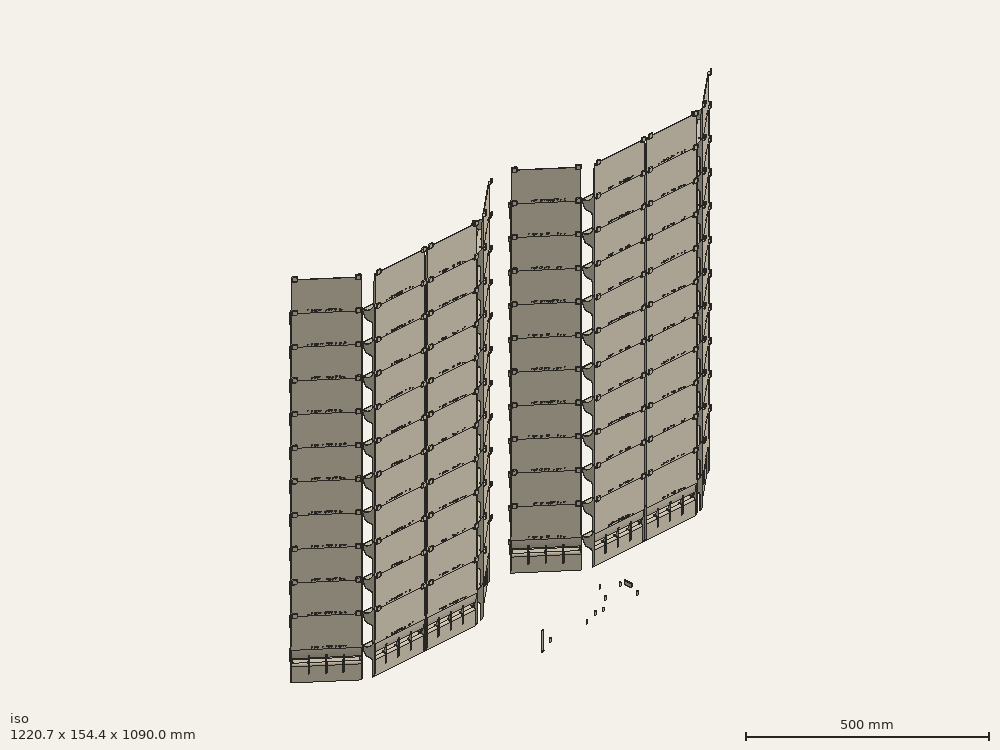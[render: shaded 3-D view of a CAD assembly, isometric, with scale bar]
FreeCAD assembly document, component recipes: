
FREECAD ASSEMBLY — COMPONENT RECIPES ("composit_stand8")

This assembly document has 28 components, labeled P0..P27 below (a component is one placed body or linked part). 26 of them carry a construction recipe — the FreeCAD feature program that regenerates the part from scratch, quoted from this document or its linked companion documents; the rest are supplied as boundary geometry only. No exploded tour is included for this assembly.
NOTE — this tour is split across 2 documents so each fits a 32k-token context. This is document 1: the component sections continue in the remaining 1 document, each repeating the header above.
COMPONENT P0 — recipe-attached ("sink", modeled in this document).
Construction recipe (the document's own serialized feature program — sketch geometry with constraints, then the solid features built on it; lengths are millimeters unless a unit is written):

FEATURE [PartDesign::SubShapeBinder] Binder001
  BindCopyOnChange = 0
  BindMode = 0
  ClaimChildren = true
  Context = -> Body003 [Binder001.]
  Fuse = false
  MakeFace = true
  OffsetFill = false
  OffsetIntersection = false
  OffsetJoinType = 0
  OffsetOpenResult = false
  PartialLoad = false
  Relative = false
  Support = -> [Sketch]
  _Version = 2
FEATURE [PartDesign::CoordinateSystem] Local_CS
  AttacherType = Attacher::AttachEngine3D
  AttachmentOffset = pos=(0,0,0) rot=(0,1,0;1.5708rad)
  MapMode = 7
  Placement = pos=(164.635,-1.4e-14,0) rot=(0.889126,0.323616,0.323616;1.68804rad)
FEATURE [Sketcher::SketchObject] Sketch005  label="sink_side_line"
  ExternalGeometry = -> [Binder001]
  FullyConstrained = true
  MapMode = 5
  Placement = pos=(164.635,-2.8e-14,0) rot=(0.889126,0.323616,0.323616;1.68804rad)
  sketch-geometry (1):
    g0: LineSegment StartX=-2.84e-14 StartY=0 StartZ=0 EndX=202.244 EndY=20 EndZ=0
  constraints (4):
    c: Coincident(g0,g-3)
    c: Vertical(g0,g-3)
    c: DistanceY(g0) = 20  'height'
    c: Angle(g0) = 0.0985699  'angle'
FEATURE [Sketcher::SketchObject] Sketch006  label="sink_front_bend_sketch"
  ExternalGeometry = -> [Sketch005]
  FullyConstrained = true
  MapMode = 5
  Placement = pos=(0,0,0) rot=(0.57735,0.57735,0.57735;2.0944rad)
  sketch-geometry (3):
    g0: LineSegment StartX=0 StartY=2.91403 StartZ=0 EndX=-1.83e-14 EndY=0 EndZ=0
    g1: LineSegment StartX=-1.83e-14 StartY=0 StartZ=0 EndX=2.88014 EndY=0.443099 EndZ=0
    g2: ArcOfCircle CenterX=2.5 CenterY=2.91403 CenterZ=0 NormalX=0 NormalY=0 NormalZ=1 AngleXU=0 Radius=2.5 StartAngle=3.14159 EndAngle=4.86504
  constraints (8):
    c: PointOnObject(g0,g-2)
    c: Coincident(g0,g-3)
    c: Coincident(g0,g1)
    c: PointOnObject(g1,g-3)
    c: Tangent(g2,g1) = -1.5708
    c: Tangent(g2,g0) = -1.5708
    c: Radius(g2) = 2.5
    c: Angle(g1) = 0.152649  'angle'
FEATURE [Sketcher::SketchObject] Sketch007
  ExternalGeometry = -> [Binder001]
  FullyConstrained = true
  MapMode = 7
  Placement = pos=(164.635,-8.5e-14,-4e-15) rot=(0.846388,-0.394677,-0.357572;1.83324rad)
  sketch-geometry (3):
    g0: ArcOfCircle CenterX=-2.5 CenterY=2.81034 CenterZ=0 NormalX=0 NormalY=0 NormalZ=1 AngleXU=0 Radius=2.5 StartAngle=4.59564 EndAngle=6.28319
    g1: LineSegment StartX=-2.79121 StartY=0.327355 StartZ=0 EndX=0 EndY=0 EndZ=0
    g2: LineSegment StartX=0 StartY=0 StartZ=0 EndX=0 EndY=2.81034 EndZ=0
  constraints (7):
    c: PointOnObject(g0,g-2)
    c: Coincident(g1,g-1)
    c: Coincident(g2,g1)
    c: Tangent(g2,g0) = -1.5708
    c: Tangent(g1,g0) = -1.5708
    c: PointOnObject(g0,g-3)
    c: Radius(g0) = 2.5
FEATURE [PartDesign::CoordinateSystem] Local_CS001
  AttacherType = Attacher::AttachEngine3D
  AttachmentOffset = pos=(0,0,0) rot=(1,0,0;0.152649rad)
  MapMode = 5
  Placement = pos=(0,0,0) rot=(1,0,0;0.152649rad)
  expr: .AttachmentOffset.Rotation.Angle = <<sink_front_bend_sketch>>.Constraints.angle
FEATURE [Sketcher::SketchObject] Sketch008  label="sink_plane_sketch"
  ExternalGeometry = -> [Sketch006,Sketch005,Sketch007]
  FullyConstrained = true
  MapMode = 5
  Placement = pos=(0,0,0) rot=(1,0,0;0.152649rad)
  sketch-geometry (4):
    g0: LineSegment StartX=-163.725 StartY=2.91403 StartZ=0 EndX=163.725 EndY=2.91403 EndZ=0
    g1: LineSegment StartX=163.725 StartY=2.91403 StartZ=0 EndX=317.576 EndY=133.529 EndZ=0
    g2: LineSegment StartX=317.576 StartY=133.529 StartZ=0 EndX=-317.576 EndY=133.529 EndZ=0
    g3: LineSegment StartX=-317.576 StartY=133.529 StartZ=0 EndX=-163.725 EndY=2.91403 EndZ=0
  constraints (14):
    c: Coincident(g0,g1)
    c: Coincident(g1,g2)
    c: Coincident(g2,g3)
    c: Coincident(g3,g0)
    c: Symmetric(g0,g0,g-2)
    c: Symmetric(g2,g1,g-2)
    c: Parallel(g1,g-4)
    c: PointOnObject(g-5,g1)
    c: PointOnObject(g-3,g0)
    c: Distance(g1) = 201.818  'rigth_side'
    c: Distance(g0) = 327.45  'front'
    c: Distance(g2) = 635.153  'end'
    c: Distance(g3) = 201.818  'left_side'
    c: DistanceY(g-4,g1) = 2
FEATURE [Sketcher::SketchObject] Sketch009
  ExternalGeometry = -> [Sketch006]
  FullyConstrained = true
  MapMode = 2
  Placement = pos=(0,0,0) rot=(0.57735,0.57735,0.57735;2.0944rad)
  sketch-geometry (4):
    g0: ArcOfCircle CenterX=2.5 CenterY=2.91403 CenterZ=0 NormalX=0 NormalY=0 NormalZ=1 AngleXU=0 Radius=2.5 StartAngle=3.14159 EndAngle=4.86504
    g1: LineSegment StartX=2.88014 StartY=0.443099 StartZ=0 EndX=2.80411 EndY=0.937285 EndZ=0
    g2: LineSegment StartX=1.1302e-12 StartY=2.91403 StartZ=0 EndX=0.5 EndY=2.91403 EndZ=0
    g3: ArcOfCircle CenterX=2.5 CenterY=2.91403 CenterZ=0 NormalX=0 NormalY=0 NormalZ=1 AngleXU=0 Radius=2 StartAngle=3.14159 EndAngle=4.86504
  constraints (10):
    c: Coincident(g0,g-3)
    c: Tangent(g0,g-3) = -1.5708
    c: Coincident(g0,g1)
    c: Coincident(g0,g2)
    c: Coincident(g3,g0)
    c: Coincident(g3,g2)
    c: Coincident(g3,g1)
    c: Perpendicular(g3,g1)
    c: Perpendicular(g3,g2)
    c: Distance(g1) = 0.5
FEATURE [Sketcher::SketchObject] Sketch010
  ExternalGeometry = -> [Sketch007]
  FullyConstrained = true
  MapMode = 7
  Placement = pos=(163.725,2.88014,0.443099) rot=(0.846388,-0.394677,-0.357572;1.83324rad)
  sketch-geometry (4):
    g0: ArcOfCircle CenterX=0.291206 CenterY=2.48298 CenterZ=0 NormalX=0 NormalY=0 NormalZ=1 AngleXU=0 Radius=2.5 StartAngle=4.59564 EndAngle=6.28319
    g1: LineSegment StartX=-2.56e-14 StartY=2.7e-15 StartZ=0 EndX=0.0582413 EndY=0.496596 EndZ=0
    g2: LineSegment StartX=2.79121 StartY=2.48298 StartZ=0 EndX=2.29121 EndY=2.48298 EndZ=0
    g3: ArcOfCircle CenterX=0.291206 CenterY=2.48298 CenterZ=0 NormalX=0 NormalY=0 NormalZ=1 AngleXU=0 Radius=2 StartAngle=4.59564 EndAngle=6.28319
  constraints (10):
    c: Coincident(g0,g-3)
    c: Tangent(g0,g-3) = -1.5708
    c: Coincident(g1,g0)
    c: Coincident(g2,g0)
    c: Coincident(g3,g0)
    c: Coincident(g3,g1)
    c: Coincident(g3,g2)
    c: Perpendicular(g0,g1)
    c: Perpendicular(g0,g2)
    c: Distance(g1) = 0.5
FEATURE [Sketcher::SketchObject] Sketch011
  ExternalGeometry = -> [Sketch008]
  FullyConstrained = true
  MapMode = 7
  Placement = pos=(-163.725,2.88014,0.443099) rot=(-0.298783,0.640743,0.707232;3.7787rad)
  sketch-geometry (4):
    g0: ArcOfCircle CenterX=0.291206 CenterY=2.48298 CenterZ=0 NormalX=0 NormalY=0 NormalZ=1 AngleXU=0 Radius=2 StartAngle=4.59564 EndAngle=6.28319
    g1: ArcOfCircle CenterX=0.291206 CenterY=2.48298 CenterZ=0 NormalX=0 NormalY=0 NormalZ=1 AngleXU=0 Radius=2.5 StartAngle=4.59564 EndAngle=6.28319
    g2: LineSegment StartX=-4e-16 StartY=0 StartZ=0 EndX=0.0582413 EndY=0.496596 EndZ=0
    g3: LineSegment StartX=2.29121 StartY=2.48298 StartZ=0 EndX=2.79121 EndY=2.48298 EndZ=0
  constraints (12):
    c: Coincident(g1,g0)
    c: Coincident(g1,g-1)
    c: Coincident(g2,g1)
    c: Coincident(g2,g0)
    c: Coincident(g3,g0)
    c: Coincident(g3,g1)
    c: Perpendicular(g0,g3)
    c: Perpendicular(g0,g2)
    c: Perpendicular(g2,g-3)
    c: Horizontal(g3)
    c: Radius(g0) = 2
    c: Distance(g2) = 0.5
FEATURE [PartDesign::Pad] Pad
  Direction = (0,-0.152057,0.988372)
  Length = 0.5
  Length2 = 10
  Placement = pos=(0,0,0) rot=(1,0,0;0.152649rad)
  Profile = -> Sketch008
  ReferenceAxis = -> Sketch008 [N_Axis]
  Suppressed = false
  Type = 0
FEATURE [PartDesign::Pad] Pad001
  BaseFeature = -> Pad
  Direction = (-0.762326,-0.639667,-0.0984104)
  Length = 201.818
  Length2 = 10
  Placement = pos=(0,0,0) rot=(1,0,0;0.152649rad)
  Profile = -> Sketch010
  ReferenceAxis = -> Sketch010 [N_Axis]
  Reversed = true
  Suppressed = false
  Type = 0
  expr: Length = <<sink_plane_sketch>>.Constraints.rigth_side
FEATURE [PartDesign::Pad] Pad002
  BaseFeature = -> Pad001
  Direction = (-0.762326,0.639667,0.0984104)
  Length = 201.818
  Length2 = 10
  Placement = pos=(0,0,0) rot=(1,0,0;0.152649rad)
  Profile = -> Sketch011
  ReferenceAxis = -> Sketch011 [N_Axis]
  Suppressed = false
  Type = 0
  expr: Length = <<sink_plane_sketch>>.Constraints.left_side
FEATURE [PartDesign::Pad] Pad003
  BaseFeature = -> Pad002
  Direction = (1,0,0)
  Length = 327.45
  Length2 = 10
  Midplane = true
  Placement = pos=(0,0,0) rot=(1,0,0;0.152649rad)
  Profile = -> Sketch009
  ReferenceAxis = -> Sketch009 [N_Axis]
  Suppressed = false
  Type = 0
  expr: Length = <<sink_plane_sketch>>.Constraints.front
FEATURE [Sketcher::SketchObject] Sketch013
  ExternalGeometry = -> [Sketch008,Sketch009]
  FullyConstrained = true
  MapMode = 5
  Placement = pos=(0,0,0) rot=(1,0,0;1.5708rad)
  sketch-geometry (6):
    g0: LineSegment StartX=-163.725 StartY=2.91403 StartZ=0 EndX=-163.725 EndY=80 EndZ=0
    g1: LineSegment StartX=-163.725 StartY=80 StartZ=0 EndX=163.725 EndY=80 EndZ=0
    g2: LineSegment StartX=163.725 StartY=80 StartZ=0 EndX=163.725 EndY=2.91403 EndZ=0
    g3: LineSegment StartX=163.725 StartY=2.91403 StartZ=0 EndX=-163.725 EndY=2.91403 EndZ=0
    g4: LineSegment StartX=-163.725 StartY=0.443099 StartZ=0 EndX=-163.725 EndY=2.91403 EndZ=0
    g5: LineSegment StartX=163.725 StartY=0.443099 StartZ=0 EndX=163.725 EndY=2.91403 EndZ=0
  constraints (16):
    c: Vertical(g0)
    c: Coincident(g0,g1)
    c: Horizontal(g1)
    c: Coincident(g1,g2)
    c: Vertical(g2)
    c: Coincident(g2,g3)
    c: Coincident(g3,g0)
    c: Horizontal(g3)
    c: PointOnObject(g-4,g3)
    c: Coincident(g4,g-3)
    c: Coincident(g4,g0)
    c: Perpendicular(g3,g4)
    c: Coincident(g5,g-3)
    c: Coincident(g5,g2)
    c: Perpendicular(g3,g5)
    c: DistanceY(g1) = 80
FEATURE [Sketcher::SketchObject] Sketch012
  ExternalGeometry = -> [Sketch008,Sketch010,Sketch013]
  FullyConstrained = true
  MapMode = 5
  Placement = pos=(164.635,-2.8e-14,0) rot=(0.889126,0.323616,0.323616;1.68804rad)
  sketch-geometry (4):
    g0: LineSegment StartX=0.909926 StartY=2.91403 StartZ=0 EndX=201.749 EndY=22.775 EndZ=0
    g1: LineSegment StartX=0.909926 StartY=2.91403 StartZ=0 EndX=0.909926 EndY=80 EndZ=0
    g2: LineSegment StartX=0.909926 StartY=80 StartZ=0 EndX=201.749 EndY=80 EndZ=0
    g3: LineSegment StartX=201.749 StartY=80 StartZ=0 EndX=201.749 EndY=22.775 EndZ=0
  constraints (11):
    c: Coincident(g0,g-4)
    c: Parallel(g-3,g0)
    c: Equal(g0,g-3)
    c: Coincident(g0,g1)
    c: Vertical(g1)
    c: Coincident(g1,g2)
    c: Horizontal(g2)
    c: Coincident(g2,g3)
    c: Coincident(g3,g0)
    c: Vertical(g3)
    c: Horizontal(g-5,g1)
FEATURE [PartDesign::Pad] Pad004
  BaseFeature = -> Pad003
  Direction = (0,-1,2e-16)
  Length = 0.5
  Length2 = 10
  Placement = pos=(0,0,0) rot=(1,0,0;0.152649rad)
  Profile = -> Sketch013
  ReferenceAxis = -> Sketch013 [N_Axis]
  Reversed = true
  Suppressed = false
  Type = 0
FEATURE [PartDesign::Pad] Pad005
  BaseFeature = -> Pad004
  Direction = (0.642788,-0.766044,-2e-16)
  Length = 0.5
  Length2 = 10
  Placement = pos=(0,0,0) rot=(1,0,0;0.152649rad)
  Profile = -> Sketch012
  ReferenceAxis = -> Sketch012 [N_Axis]
  Reversed = true
  Suppressed = false
  Type = 0
FEATURE [Sketcher::SketchObject] Sketch014
  ExternalGeometry = -> [Binder001]
  FullyConstrained = true
  MapMode = 5
  sketch-geometry (1):
    g0: LineSegment StartX=-319.563 StartY=130 StartZ=0 EndX=-164.635 EndY=0 EndZ=0
  constraints (2):
    c: Symmetric(g0,g-3,g-2)
    c: Symmetric(g0,g-3,g-2)
FEATURE [PartDesign::CoordinateSystem] Local_CS003
  AttacherType = Attacher::AttachEngine3D
  AttachmentOffset = pos=(0,0,0) rot=(0,1,0;1.5708rad)
  MapMode = 7
  Placement = pos=(-164.635,-1.4e-14,0) rot=(0.889126,-0.323616,-0.323616;1.68804rad)
FEATURE [Sketcher::SketchObject] Sketch015
  ExternalGeometry = -> [Sketch008,Sketch011,Sketch013]
  FullyConstrained = true
  MapMode = 5
  Placement = pos=(-164.635,-2.8e-14,0) rot=(0.889126,-0.323616,-0.323616;1.68804rad)
  sketch-geometry (5):
    g0: LineSegment StartX=-201.749 StartY=22.775 StartZ=0 EndX=-0.909926 EndY=2.91403 EndZ=0
    g1: LineSegment StartX=-0.909926 StartY=2.91403 StartZ=0 EndX=-0.909926 EndY=80 EndZ=0
    g2: LineSegment StartX=-0.909926 StartY=80 StartZ=0 EndX=-201.749 EndY=80 EndZ=0
    g3: LineSegment StartX=-201.749 StartY=80 StartZ=0 EndX=-201.749 EndY=22.775 EndZ=0
    g4: LineSegment StartX=-201.993 StartY=20.3041 StartZ=0 EndX=-201.749 EndY=22.775 EndZ=0
  constraints (13):
    c: Coincident(g0,g-4)
    c: Coincident(g1,g0)
    c: Vertical(g1)
    c: Coincident(g1,g2)
    c: Horizontal(g2)
    c: Coincident(g2,g3)
    c: Coincident(g3,g0)
    c: Vertical(g3)
    c: Coincident(g4,g-3)
    c: Coincident(g4,g0)
    c: Perpendicular(g-3,g4)
    c: Parallel(g-3,g0)
    c: Horizontal(g1,g-5)
FEATURE [PartDesign::Pad] Pad006
  BaseFeature = -> Pad005
  Direction = (-0.642788,-0.766044,-2e-16)
  Length = 0.5
  Length2 = 10
  Placement = pos=(0,0,0) rot=(1,0,0;0.152649rad)
  Profile = -> Sketch015
  ReferenceAxis = -> Sketch015 [N_Axis]
  Reversed = true
  Suppressed = false
  Type = 0
FEATURE [Sketcher::SketchObject] Sketch016
  ExternalGeometry = -> [Pad006]
  FullyConstrained = true
  MapMode = 5
  Placement = pos=(0,0,0) rot=(1,0,0;0.152649rad)
  sketch-geometry (28):
    g0: LineSegment StartX=0 StartY=2 StartZ=0 EndX=40.9313 EndY=2 EndZ=0
    g1: LineSegment StartX=40.9313 StartY=2 StartZ=0 EndX=81.8625 EndY=2 EndZ=0
    g2: LineSegment StartX=81.8625 StartY=2 StartZ=0 EndX=122.794 EndY=2 EndZ=0
    g3: LineSegment StartX=122.794 StartY=2 StartZ=0 EndX=163.725 EndY=2 EndZ=0
    g4: ArcOfCircle CenterX=-17 CenterY=2 CenterZ=0 NormalX=0 NormalY=0 NormalZ=1 AngleXU=0 Radius=3 StartAngle=1.5708 EndAngle=4.71239
    g5: ArcOfCircle CenterX=17 CenterY=2 CenterZ=0 NormalX=0 NormalY=0 NormalZ=1 AngleXU=0 Radius=3 StartAngle=4.71239 EndAngle=7.85398
    g6: LineSegment StartX=-17 StartY=5 StartZ=0 EndX=17 EndY=5 EndZ=0
    g7: LineSegment StartX=-17 StartY=-1 StartZ=0 EndX=17 EndY=-1 EndZ=0
    g8: GeomPoint X=-20 Y=2 Z=0
    g9: GeomPoint X=20 Y=2 Z=0
    g10: ArcOfCircle CenterX=106 CenterY=2 CenterZ=0 NormalX=0 NormalY=0 NormalZ=1 AngleXU=0 Radius=3 StartAngle=1.5708 EndAngle=4.71239
    g11: ArcOfCircle CenterX=140 CenterY=2 CenterZ=0 NormalX=0 NormalY=0 NormalZ=1 AngleXU=0 Radius=3 StartAngle=4.71239 EndAngle=7.85398
    g12: LineSegment StartX=106 StartY=5 StartZ=0 EndX=140 EndY=5 EndZ=0
    g13: LineSegment StartX=106 StartY=-1 StartZ=0 EndX=140 EndY=-1 EndZ=0
    g14: ArcOfCircle CenterX=-140 CenterY=2 CenterZ=0 NormalX=0 NormalY=0 NormalZ=1 AngleXU=0 Radius=3 StartAngle=1.5708 EndAngle=4.71239
    g15: ArcOfCircle CenterX=-106 CenterY=2 CenterZ=0 NormalX=0 NormalY=0 NormalZ=1 AngleXU=0 Radius=3 StartAngle=4.71239 EndAngle=7.85398
    g16: LineSegment StartX=-140 StartY=5 StartZ=0 EndX=-106 EndY=5 EndZ=0
    g17: LineSegment StartX=-140 StartY=-1 StartZ=0 EndX=-106 EndY=-1 EndZ=0
    g18: ArcOfCircle CenterX=-78.5 CenterY=2 CenterZ=0 NormalX=0 NormalY=0 NormalZ=1 AngleXU=0 Radius=3 StartAngle=1.5708 EndAngle=4.71239
    g19: ArcOfCircle CenterX=-44.5 CenterY=2 CenterZ=0 NormalX=0 NormalY=0 NormalZ=1 AngleXU=0 Radius=3 StartAngle=4.71239 EndAngle=7.85398
    g20: LineSegment StartX=-78.5 StartY=5 StartZ=0 EndX=-44.5 EndY=5 EndZ=0
    g21: LineSegment StartX=-78.5 StartY=-1 StartZ=0 EndX=-44.5 EndY=-1 EndZ=0
    g22: ArcOfCircle CenterX=44.5 CenterY=2 CenterZ=0 NormalX=0 NormalY=0 NormalZ=1 AngleXU=0 Radius=3 StartAngle=1.5708 EndAngle=4.71239
    g23: ArcOfCircle CenterX=78.5 CenterY=2 CenterZ=0 NormalX=0 NormalY=0 NormalZ=1 AngleXU=0 Radius=3 StartAngle=4.71239 EndAngle=7.85398
    g24: LineSegment StartX=44.5 StartY=5 StartZ=0 EndX=78.5 EndY=5 EndZ=0
    g25: LineSegment StartX=44.5 StartY=-1 StartZ=0 EndX=78.5 EndY=-1 EndZ=0
    g26: LineSegment StartX=17 StartY=-1 StartZ=0 EndX=44.5 EndY=-1 EndZ=0
    g27: LineSegment StartX=78.5 StartY=-1 StartZ=0 EndX=106 EndY=-1 EndZ=0
  constraints (67):
    c: PointOnObject(g0,g-2)
    c: Coincident(g0,g1)
    c: Horizontal(g1)
    c: Coincident(g1,g2)
    c: Coincident(g2,g3)
    c: Horizontal(g3)
    c: Vertical(g-3,g3)
    c: Horizontal(g0)
    c: Equal(g0,g1)
    c: Equal(g1,g2)
    c: Equal(g2,g3)
    c: DistanceY(g0) = 2
    c: Horizontal(g2)
    c: Tangent(g4,g6) = 1.5708
    c: Tangent(g4,g7) = -1.5708
    c: Tangent(g5,g6) = 1.5708
    c: Tangent(g5,g7) = -1.5708
    c: Equal(g4,g5)
    c: PointOnObject(g5,g0)
    c: Symmetric(g4,g5,g-2)
    c: Radius(g5) = 3
    c: PointOnObject(g8,g4)
    c: PointOnObject(g9,g5)
    c: Horizontal(g9,g8)
    c: Horizontal(g8,g0)
    c: DistanceX(g8,g9) = 40
    c: Tangent(g10,g12) = 1.5708
    c: Tangent(g10,g13) = -1.5708
    c: Tangent(g11,g12) = 1.5708
    c: Tangent(g11,g13) = -1.5708
    c: Equal(g10,g11)
    c: Tangent(g14,g16) = 1.5708
    c: Tangent(g14,g17) = -1.5708
    c: Tangent(g15,g16) = 1.5708
    c: Tangent(g15,g17) = -1.5708
    c: Equal(g14,g15)
    c: Tangent(g18,g20) = 1.5708
    c: Tangent(g18,g21) = -1.5708
    c: Tangent(g19,g20) = 1.5708
    c: Tangent(g19,g21) = -1.5708
    c: Equal(g18,g19)
    c: Tangent(g22,g24) = 1.5708
    c: Tangent(g22,g25) = -1.5708
    c: Tangent(g23,g24) = 1.5708
    c: Tangent(g23,g25) = -1.5708
    c: Equal(g22,g23)
    c: Horizontal(g14,g15)
    c: Horizontal(g18,g19)
    c: Horizontal(g22,g23)
    c: Horizontal(g10,g11)
    c: Equal(g11,g23)
    c: Equal(g23,g5)
    c: Equal(g5,g19)
    c: Equal(g19,g15)
    c: Equal(g16,g20)
    c: Equal(g20,g6)
    c: Equal(g6,g24)
    c: Equal(g12,g24)
    c: Horizontal(g10,g22)
    c: Symmetric(g19,g22,g-2)
    c: Symmetric(g10,g15,g-2)
    c: Tangent(g26,g5) = -1.5708
    c: Coincident(g26,g22)
    c: Coincident(g27,g23)
    c: Coincident(g27,g10)
    c: Equal(g26,g27)
    c: DistanceX(g11) = 140
FEATURE [PartDesign::FeaturePython] SketchOnSheet  # WARN: FeaturePython — macro-defined, semantics opaque (R4)
  BaseFeature = -> Pad006
  Sketch = -> Sketch016
  Suppressed = false
  baseObject = -> Pad006 [Face14]
  kfactor = 0.5
FEATURE [PartDesign::FeaturePython] CornerRelief  # WARN: FeaturePython — macro-defined, semantics opaque (R4)
  BaseFeature = -> SketchOnSheet
  ReliefSketch = 0
  Size = 5
  SizeRatio = 1
  Suppressed = false
  XOffset = 0
  YOffset = 0
  baseObject = -> SketchOnSheet [Edge56,Edge57]
  kfactor = 0.5
FEATURE [PartDesign::FeaturePython] CornerRelief001  # WARN: FeaturePython — macro-defined, semantics opaque (R4)
  BaseFeature = -> CornerRelief
  ReliefSketch = 0
  Size = 5
  SizeRatio = 1
  Suppressed = false
  XOffset = 0
  YOffset = 0
  baseObject = -> CornerRelief [Edge17,Edge14]
  kfactor = 0.5
  expr: Size = <<CornerRelief>>.Size
FEATURE [Sketcher::SketchObject] Sketch017
  ExternalGeometry = -> [Sketch012]
  FullyConstrained = true
  MapMode = 5
  Placement = pos=(164.635,-2.8e-14,0) rot=(0.889126,0.323616,0.323616;1.68804rad)
  sketch-geometry (6):
    g0: LineSegment StartX=0.909926 StartY=78 StartZ=0 EndX=0.909926 EndY=80 EndZ=0
    g1: LineSegment StartX=0.909926 StartY=80 StartZ=0 EndX=2.90993 EndY=80 EndZ=0
    g2: LineSegment StartX=199.749 StartY=80 StartZ=0 EndX=201.749 EndY=80 EndZ=0
    g3: LineSegment StartX=201.749 StartY=80 StartZ=0 EndX=201.749 EndY=78 EndZ=0
    g4: ArcOfCircle CenterX=2.90993 CenterY=78 CenterZ=0 NormalX=0 NormalY=0 NormalZ=1 AngleXU=0 Radius=2 StartAngle=1.5708 EndAngle=3.14159
    g5: ArcOfCircle CenterX=199.749 CenterY=78 CenterZ=0 NormalX=0 NormalY=0 NormalZ=1 AngleXU=0 Radius=2 StartAngle=5.856e-13 EndAngle=1.5708
  constraints (14):
    c: Coincident(g0,g-3)
    c: Vertical(g0)
    c: Coincident(g0,g1)
    c: PointOnObject(g1,g-3)
    c: Coincident(g2,g-3)
    c: Coincident(g2,g3)
    c: Tangent(g5,g3) = 1.5708
    c: Tangent(g5,g2) = 1.5708
    c: Tangent(g4,g1) = 1.5708
    c: Tangent(g4,g0) = 1.5708
    c: Equal(g4,g5)
    c: Radius(g5) = 2
    c: Vertical(g3)
    c: PointOnObject(g2,g-3)
FEATURE [Sketcher::SketchObject] Sketch018
  ExternalGeometry = -> [Sketch015]
  FullyConstrained = true
  MapMode = 2
  Placement = pos=(-164.635,-2.8e-14,0) rot=(0.889126,-0.323616,-0.323616;1.68804rad)
  sketch-geometry (6):
    g0: ArcOfCircle CenterX=-2.90993 CenterY=78 CenterZ=0 NormalX=0 NormalY=0 NormalZ=1 AngleXU=0 Radius=2 StartAngle=6.28318 EndAngle=7.85398
    g1: ArcOfCircle CenterX=-199.749 CenterY=78 CenterZ=0 NormalX=0 NormalY=0 NormalZ=1 AngleXU=0 Radius=2 StartAngle=1.5708 EndAngle=3.14159
    g2: LineSegment StartX=-201.749 StartY=78 StartZ=0 EndX=-201.749 EndY=80 EndZ=0
    g3: LineSegment StartX=-201.749 StartY=80 StartZ=0 EndX=-199.749 EndY=80 EndZ=0
    g4: LineSegment StartX=-2.90993 StartY=80 StartZ=0 EndX=-0.909926 EndY=80 EndZ=0
    g5: LineSegment StartX=-0.909926 StartY=80 StartZ=0 EndX=-0.909926 EndY=78 EndZ=0
  constraints (15):
    c: PointOnObject(g1,g-3)
    c: Coincident(g2,g3)
    c: Vertical(g2)
    c: Tangent(g1,g2) = 1.5708
    c: Tangent(g3,g1) = 1.5708
    c: Coincident(g4,g5)
    c: Coincident(g5,g0)
    c: Tangent(g5,g0)
    c: Tangent(g0,g4) = 1.5708
    c: Coincident(g4,g-3)
    c: Equal(g0,g1)
    c: Radius(g0) = 2
    c: Coincident(g2,g-3)
    c: PointOnObject(g0,g-3)
    c: Vertical(g5)
FEATURE [Sketcher::SketchObject] Sketch019
  ExternalGeometry = -> [Sketch013]
  FullyConstrained = true
  MapMode = 5
  Placement = pos=(0,0,0) rot=(1,0,0;1.5708rad)
  sketch-geometry (6):
    g0: LineSegment StartX=161.725 StartY=80 StartZ=0 EndX=163.725 EndY=80 EndZ=0
    g1: LineSegment StartX=163.725 StartY=80 StartZ=0 EndX=163.725 EndY=78 EndZ=0
    g2: LineSegment StartX=-163.725 StartY=78 StartZ=0 EndX=-163.725 EndY=80 EndZ=0
    g3: LineSegment StartX=-163.725 StartY=80 StartZ=0 EndX=-161.725 EndY=80 EndZ=0
    g4: ArcOfCircle CenterX=-161.725 CenterY=78 CenterZ=0 NormalX=0 NormalY=0 NormalZ=1 AngleXU=0 Radius=2 StartAngle=1.5708 EndAngle=3.14159
    g5: ArcOfCircle CenterX=161.725 CenterY=78 CenterZ=0 NormalX=0 NormalY=0 NormalZ=1 AngleXU=0 Radius=2 StartAngle=5.87e-13 EndAngle=1.5708
  constraints (14):
    c: Coincident(g0,g-3)
    c: Coincident(g0,g1)
    c: Coincident(g2,g-3)
    c: Coincident(g2,g3)
    c: Tangent(g5,g1) = 1.5708
    c: Tangent(g5,g0) = 1.5708
    c: Tangent(g4,g2) = 1.5708
    c: Tangent(g4,g3) = 1.5708
    c: Equal(g5,g4)
    c: Radius(g5) = 2
    c: PointOnObject(g3,g-3)
    c: Vertical(g2)
    c: PointOnObject(g0,g-3)
    c: Vertical(g1)
FEATURE [PartDesign::Pocket] Pocket
  BaseFeature = -> CornerRelief001
  Direction = (-0.642788,0.766044,2e-16)
  Length = 5
  Length2 = 5
  Midplane = true
  Profile = -> Sketch017
  ReferenceAxis = -> Sketch017 [N_Axis]
  Suppressed = false
  Type = 1
FEATURE [PartDesign::Pocket] Pocket001
  BaseFeature = -> Pocket
  Direction = (0.642788,0.766044,-3e-16)
  Length = 5
  Length2 = 5
  Midplane = true
  Profile = -> Sketch018
  ReferenceAxis = -> Sketch018 [N_Axis]
  Suppressed = false
  Type = 0
FEATURE [PartDesign::Pocket] Pocket002
  BaseFeature = -> Pocket001
  Direction = (0,1,-2e-16)
  Length = 5
  Length2 = 5
  Midplane = true
  Profile = -> Sketch019
  ReferenceAxis = -> Sketch019 [N_Axis]
  Suppressed = false
  Type = 1
FEATURE [PartDesign::CoordinateSystem] Local_CS004  label="sink_place"
  AttacherType = Attacher::AttachEngine3D
  MapMode = 5
FEATURE [Sketcher::SketchObject] Sketch054
  ExternalGeometry = -> [Sketch008]
  FullyConstrained = true
  MapMode = 5
  Placement = pos=(0,0,0) rot=(0.57735,0.57735,0.57735;2.0944rad)
  sketch-geometry (7):
    g0: ArcOfCircle CenterX=132.281 CenterY=18.3274 CenterZ=0 NormalX=0 NormalY=0 NormalZ=1 AngleXU=0 Radius=2 StartAngle=0 EndAngle=1.72345
    g1: ArcOfCircle CenterX=132.281 CenterY=18.3274 CenterZ=0 NormalX=0 NormalY=0 NormalZ=1 AngleXU=0 Radius=2.5 StartAngle=1.4e-15 EndAngle=1.72345
    g2: LineSegment StartX=131.977 StartY=20.3041 StartZ=0 EndX=131.901 EndY=20.7983 EndZ=0
    g3: LineSegment StartX=134.281 StartY=18.3274 StartZ=0 EndX=134.281 EndY=10.8274 EndZ=0
    g4: LineSegment StartX=134.281 StartY=10.8274 StartZ=0 EndX=134.781 EndY=10.8274 EndZ=0
    g5: LineSegment StartX=134.781 StartY=10.8274 StartZ=0 EndX=134.781 EndY=18.3274 EndZ=0
    g6: LineSegment StartX=134.781 StartY=20.8274 StartZ=0 EndX=0 EndY=20.8274 EndZ=0
  constraints (19):
    c: Coincident(g1,g0)
    c: Coincident(g2,g1)
    c: Vertical(g3)
    c: Coincident(g4,g3)
    c: Horizontal(g4)
    c: Coincident(g5,g4)
    c: Vertical(g5)
    c: Tangent(g0,g-3) = 1.5708
    c: Perpendicular(g2,g-3)
    c: Distance(g2) = 0.5
    c: Coincident(g2,g0)
    c: Radius(g0) = 2
    c: Horizontal(g6)
    c: Tangent(g6,g1)
    c: PointOnObject(g6,g-2)
    c: PointOnObject(g6,g5)
    c: Tangent(g3,g0) = 1.5708
    c: DistanceY(g4,g6) = 10
    c: Tangent(g5,g1) = -1.5708
FEATURE [PartDesign::Pad] Pad017
  BaseFeature = -> Pocket002
  Direction = (1,0,0)
  Length = 635.153
  Length2 = 10
  Midplane = true
  Profile = -> Sketch054
  ReferenceAxis = -> Sketch054 [N_Axis]
  Suppressed = false
  Type = 0
  expr: Length = <<sink_plane_sketch>>.Constraints.end
FEATURE [Sketcher::SketchObject] Sketch055
  ExternalGeometry = -> [Sketch054]
  FullyConstrained = true
  MapMode = 5
  Placement = pos=(0,0,0) rot=(1,0,0;1.5708rad)
  expr: Constraints[5] = <<sink_plane_sketch>>.Constraints.end / 2
  sketch-geometry (3):
    g0: ArcOfCircle CenterX=315.576 CenterY=12.8274 CenterZ=0 NormalX=0 NormalY=0 NormalZ=1 AngleXU=0 Radius=2 StartAngle=4.71239 EndAngle=6.28319
    g1: LineSegment StartX=315.576 StartY=10.8274 StartZ=0 EndX=317.576 EndY=10.8274 EndZ=0
    g2: LineSegment StartX=317.576 StartY=10.8274 StartZ=0 EndX=317.576 EndY=12.8274 EndZ=0
  constraints (9):
    c: Coincident(g1,g2)
    c: Coincident(g2,g0)
    c: Tangent(g2,g0)
    c: Vertical(g2)
    c: Horizontal(g1)
    c: DistanceX(g1) = 317.576
    c: Radius(g0) = 2
    c: Tangent(g0,g1) = -1.5708
    c: Horizontal(g-3,g1)
FEATURE [PartDesign::Pocket] Pocket006
  BaseFeature = -> Pad017
  Direction = (0,1,-2e-16)
  Length = 5
  Length2 = 5
  Midplane = true
  Profile = -> Sketch055
  ReferenceAxis = -> Sketch055 [N_Axis]
  Suppressed = false
  Type = 1
FEATURE [PartDesign::Mirrored] Mirrored002
  BaseFeature = -> Pocket006
  MirrorPlane = -> Sketch055 [V_Axis]
  Originals = -> [Pocket006]
  Suppressed = false
FEATURE [PartDesign::Boolean] Boolean006
  BaseFeature = -> Mirrored002
  Group = -> [Compound014]
  Suppressed = false
  Type = 1
  UsePlacement = true
FEATURE [PartDesign::Body] Body003  label="sink"
  Group = -> [Binder001,Local_CS,Sketch005,Sketch006,Sketch007,Local_CS001,Sketch008,Sketch009,Sketch010,Sketch011,Pad,Pad001,Pad002,Pad003,Sketch012,Sketch013,Pad004,Pad005,Sketch014,Local_CS003,Sketch015,Pad006,Sketch016,SketchOnSheet,CornerRelief,CornerRelief001,Sketch017,Sketch018,Sketch019,Pocket,Pocket001,Pocket002,Local_CS004,Sketch054,Pad017,Sketch055,Pocket006,Mirrored002,Boolean006]
  Origin = -> Origin004
  Tip = -> Mirrored002
COMPONENT P1 — recipe-attached ("dropper_fix_PP", modeled in this document).
Construction recipe (the document's own serialized feature program — sketch geometry with constraints, then the solid features built on it; lengths are millimeters unless a unit is written):

FEATURE [PartDesign::SubShapeBinder] Binder007
  BindCopyOnChange = 0
  BindMode = 0
  ClaimChildren = true
  Context = -> Body004 [Binder007.]
  Fuse = false
  MakeFace = true
  OffsetFill = false
  OffsetIntersection = false
  OffsetJoinType = 0
  OffsetOpenResult = false
  PartialLoad = false
  Relative = true
  Support = -> [Connect004]
  _Version = 2
FEATURE [PartDesign::Pad] Pad007
  Direction = (0,0,1)
  Length = 5
  Length2 = 10
  Profile = -> Binder007
  Suppressed = false
  Type = 0
FEATURE [PartDesign::CoordinateSystem] Local_CS012
  AttacherType = Attacher::AttachEngine3D
  AttachmentSupport = -> [XY_Plane005]
  MapMode = 5
FEATURE [PartDesign::Boolean] Boolean003
  BaseFeature = -> Pad007
  Group = -> [Fusion]
  Suppressed = false
  Type = 1
  UsePlacement = true
FEATURE [PartDesign::Body] Body004  label="dropper_fix_PP"
  Group = -> [Binder007,Pad007,Boolean003,Local_CS012]
  Origin = -> Origin005
  Tip = -> Boolean003
COMPONENT P2 — recipe-attached ("bar", modeled in this document).
Construction recipe (the document's own serialized feature program — sketch geometry with constraints, then the solid features built on it; lengths are millimeters unless a unit is written):

FEATURE [PartDesign::SubShapeBinder] Binder008
  BindCopyOnChange = 0
  BindMode = 0
  ClaimChildren = true
  Context = -> Body005 [Binder008.]
  Fuse = false
  MakeFace = true
  OffsetFill = false
  OffsetIntersection = false
  OffsetJoinType = 0
  OffsetOpenResult = false
  PartialLoad = false
  Relative = false
  Support = -> [Connect005]
  _Version = 2
FEATURE [PartDesign::Pad] Pad008  label="bar_pad"
  Direction = (0,0,1)
  Length = 1272.25
  Length2 = 10
  Profile = -> Binder008
  Refine = true
  Suppressed = false
  Type = 0
  expr: Length = <<Dimensions>>.Constraints.width - 3 mm * 2
FEATURE [PartDesign::CoordinateSystem] Local_CS016  label="bar_orig"
  AttacherType = Attacher::AttachEngine3D
  AttachmentSupport = -> [XY_Plane006]
  MapMode = 5
FEATURE [PartDesign::CoordinateSystem] Local_CS018  label="bar_top"
  AttacherType = Attacher::AttachEngine3D
  AttachmentOffset = pos=(0,0,1272.25) rot=(0,-1,0;3.14159rad)
  AttachmentSupport = -> [XY_Plane006]
  MapMode = 5
  Placement = pos=(0,0,1272.25) rot=(0,-1,0;3.14159rad)
  expr: .AttachmentOffset.Base.z = <<bar_pad>>.Length
FEATURE [Sketcher::SketchObject] Sketch057
  AttachmentSupport = -> [XZ_Plane006]
  FullyConstrained = true
  MapMode = 5
  Placement = pos=(0,0,0) rot=(1,0,0;1.5708rad)
  expr: Constraints[6] = <<bar_base_sketch>>.Constraints.total_width / 2
  sketch-geometry (3):
    g0: ArcOfCircle CenterX=25 CenterY=5 CenterZ=0 NormalX=0 NormalY=0 NormalZ=1 AngleXU=0 Radius=5 StartAngle=4.71239 EndAngle=6.28319
    g1: LineSegment StartX=25 StartY=3.304e-13 StartZ=0 EndX=30 EndY=0 EndZ=0
    g2: LineSegment StartX=30 StartY=0 StartZ=0 EndX=30 EndY=5 EndZ=0
  constraints (8):
    c: PointOnObject(g0,g-1)
    c: PointOnObject(g1,g-1)
    c: Coincident(g2,g1)
    c: Tangent(g2,g0) = -1.5708
    c: Vertical(g2)
    c: Tangent(g1,g0) = -1.5708
    c: DistanceX(g1) = 30
    c: Radius(g0) = 5
FEATURE [PartDesign::Plane] DatumPlane001
  AttachmentOffset = pos=(0,0,636.126) rot=(0,0,1;0rad)
  AttachmentSupport = -> [XY_Plane006]
  Length = 60
  MapMode = 5
  Placement = pos=(0,0,636.126) rot=(0,0,1;0rad)
  ResizeMode = 0
  Width = 60
  expr: .AttachmentOffset.Base.z = <<bar_pad>>.Length / 2
FEATURE [PartDesign::Mirrored] Mirrored003
  MirrorPlane = -> YZ_Plane006
  Suppressed = false
FEATURE [PartDesign::Mirrored] Mirrored004
  MirrorPlane = -> DatumPlane001
  Suppressed = false
FEATURE [Sketcher::SketchObject] Sketch058
  AttachmentOffset = pos=(0,240.563,0) rot=(0,0,1;0rad)
  AttachmentSupport = -> [XZ_Plane006]
  FullyConstrained = true
  MapMode = 5
  Placement = pos=(0,5.34e-14,240.563) rot=(1,0,0;1.5708rad)
  expr: .AttachmentOffset.Base.y = <<Dimensions>>.Constraints.module_middle_side - 3 mm - <<Dimensions>>.Constraints.module_center_offset
  expr: Constraints[44] = -<<bar_base_sketch>>.Constraints.total_width / 2
  sketch-geometry (22):
    g0: LineSegment StartX=-21 StartY=61.5 StartZ=0 EndX=-21 EndY=70.5 EndZ=0
    g1: LineSegment StartX=-30 StartY=76.5 StartZ=0 EndX=-30 EndY=55.5 EndZ=0
    g2: LineSegment StartX=-21 StartY=-70.5 StartZ=0 EndX=-21 EndY=-61.5 EndZ=0
    g3: LineSegment StartX=-30 StartY=-55.5 StartZ=0 EndX=-30 EndY=-76.5 EndZ=0
    g4: LineSegment StartX=-24 StartY=-58.5 StartZ=0 EndX=-27 EndY=-58.5 EndZ=0
    g5: LineSegment StartX=-27 StartY=58.5 StartZ=0 EndX=-24 EndY=58.5 EndZ=0
    g6: LineSegment StartX=-24 StartY=73.5 StartZ=0 EndX=-27 EndY=73.5 EndZ=0
    g7: LineSegment StartX=-27 StartY=-73.5 StartZ=0 EndX=-24 EndY=-73.5 EndZ=0
    g8: ArcOfCircle CenterX=-27 CenterY=76.5 CenterZ=0 NormalX=0 NormalY=0 NormalZ=1 AngleXU=0 Radius=3 StartAngle=3.14159 EndAngle=4.71239
    g9: ArcOfCircle CenterX=-27 CenterY=55.5 CenterZ=0 NormalX=0 NormalY=0 NormalZ=1 AngleXU=0 Radius=3 StartAngle=1.5708 EndAngle=3.14159
    g10: ArcOfCircle CenterX=-27 CenterY=-55.5 CenterZ=0 NormalX=0 NormalY=0 NormalZ=1 AngleXU=0 Radius=3 StartAngle=3.14159 EndAngle=4.71239
    g11: ArcOfCircle CenterX=-27 CenterY=-76.5 CenterZ=0 NormalX=0 NormalY=0 NormalZ=1 AngleXU=0 Radius=3 StartAngle=1.5708 EndAngle=3.14159
    g12: ArcOfCircle CenterX=-24 CenterY=61.5 CenterZ=0 NormalX=0 NormalY=0 NormalZ=1 AngleXU=0 Radius=3 StartAngle=4.71239 EndAngle=6.28319
    g13: GeomPoint X=-21 Y=58.5 Z=0
    g14: ArcOfCircle CenterX=-24 CenterY=70.5 CenterZ=0 NormalX=0 NormalY=0 NormalZ=1 AngleXU=0 Radius=3 StartAngle=1.6e-15 EndAngle=1.5708
    g15: GeomPoint X=-21 Y=73.5 Z=0
    g16: ArcOfCircle CenterX=-24 CenterY=-61.5 CenterZ=0 NormalX=0 NormalY=0 NormalZ=1 AngleXU=0 Radius=3 StartAngle=9e-16 EndAngle=1.5708
    g17: GeomPoint X=-21 Y=-58.5 Z=0
    g18: ArcOfCircle CenterX=-24 CenterY=-70.5 CenterZ=0 NormalX=0 NormalY=0 NormalZ=1 AngleXU=0 Radius=3 StartAngle=4.71239 EndAngle=6.28319
    g19: GeomPoint X=-21 Y=-73.5 Z=0
    g20: GeomPoint X=-30 Y=66 Z=0
    g21: GeomPoint X=-30 Y=-66 Z=0
  constraints (49):
    c: Vertical(g0)
    c: Vertical(g1)
    c: Vertical(g2)
    c: Vertical(g3)
    c: Equal(g3,g1)
    c: Symmetric(g3,g1,g-1)
    c: Horizontal(g4)
    c: Horizontal(g5)
    c: Horizontal(g6)
    c: Horizontal(g7)
    c: Tangent(g11,g7) = 1.5708
    c: Tangent(g11,g3) = -1.5708
    c: Tangent(g10,g4) = 1.5708
    c: Tangent(g10,g3) = -1.5708
    c: Tangent(g9,g5) = 1.5708
    c: Tangent(g9,g1) = -1.5708
    c: Tangent(g8,g6) = 1.5708
    c: Tangent(g8,g1) = -1.5708
    c: PointOnObject(g13,g0)
    c: PointOnObject(g13,g5)
    c: Tangent(g0,g12) = -1.5708
    c: Tangent(g5,g12) = -1.5708
    c: PointOnObject(g15,g0)
    c: PointOnObject(g15,g6)
    c: Tangent(g0,g14) = -1.5708
    c: Tangent(g6,g14) = -1.5708
    c: PointOnObject(g17,g2)
    c: PointOnObject(g17,g4)
    c: Tangent(g2,g16) = -1.5708
    c: Tangent(g4,g16) = -1.5708
    c: PointOnObject(g19,g2)
    c: PointOnObject(g19,g7)
    c: Tangent(g2,g18) = -1.5708
    c: Tangent(g7,g18) = -1.5708
    c: Equal(g18,g11)
    c: Equal(g11,g16)
    c: Equal(g16,g10)
    c: Equal(g10,g9)
    c: Equal(g9,g12)
    c: Equal(g12,g14)
    c: Equal(g14,g8)
    c: Radius(g14) = 3
    c: Symmetric(g3,g3,g21)
    c: Symmetric(g1,g1,g20)
    c: DistanceX(g20) = -30
    c: Vertical(g17,g13)
    c: DistanceY(g19,g17) = 15
    c: DistanceY(g21,g20) = 132
    c: Distance(g15,g1) = 9
FEATURE [PartDesign::Boolean] Boolean004
  BaseFeature = -> Pad008
  Group = -> [Compound012]
  Refine = true
  Suppressed = false
  Type = 1
  UsePlacement = true
FEATURE [PartDesign::Pocket] Pocket007
  BaseFeature = -> Boolean004
  Direction = (0,1,-2e-16)
  Length = 5
  Length2 = 5
  Profile = -> Sketch057
  ReferenceAxis = -> Sketch057 [N_Axis]
  Suppressed = false
  Type = 1
FEATURE [PartDesign::MultiTransform] MultiTransform
  BaseFeature = -> Pocket007
  Originals = -> [Pocket007]
  Suppressed = false
  Transformations = -> [Mirrored003,Mirrored004]
FEATURE [Sketcher::SketchObject] Sketch113
  AttachmentOffset = pos=(0,97,0) rot=(0,0,1;0rad)
  AttachmentSupport = -> [XZ_Plane006]
  FullyConstrained = true
  MapMode = 5
  Placement = pos=(0,2.15e-14,97) rot=(1,0,0;1.5708rad)
  sketch-geometry (10):
    g0: LineSegment StartX=-18.1 StartY=-50 StartZ=0 EndX=-13 EndY=-50 EndZ=0
    g1: LineSegment StartX=-11 StartY=-48 StartZ=0 EndX=-11 EndY=48 EndZ=0
    g2: LineSegment StartX=-13 StartY=50 StartZ=0 EndX=-18.1 EndY=50 EndZ=0
    g3: LineSegment StartX=-20.1 StartY=48 StartZ=0 EndX=-20.1 EndY=-48 EndZ=0
    g4: ArcOfCircle CenterX=-18.1 CenterY=-48 CenterZ=0 NormalX=0 NormalY=0 NormalZ=1 AngleXU=0 Radius=2 StartAngle=3.14159 EndAngle=4.71239
    g5: ArcOfCircle CenterX=-13 CenterY=-48 CenterZ=0 NormalX=0 NormalY=0 NormalZ=1 AngleXU=0 Radius=2 StartAngle=4.71239 EndAngle=6.28319
    g6: ArcOfCircle CenterX=-13 CenterY=48 CenterZ=0 NormalX=0 NormalY=0 NormalZ=1 AngleXU=0 Radius=2 StartAngle=7e-16 EndAngle=1.5708
    g7: ArcOfCircle CenterX=-18.1 CenterY=48 CenterZ=0 NormalX=0 NormalY=0 NormalZ=1 AngleXU=0 Radius=2 StartAngle=1.5708 EndAngle=3.14159
    g8: GeomPoint X=-20.1 Y=-50 Z=0
    g9: GeomPoint X=-11 Y=50 Z=0
  constraints (23):
    c: Tangent(g0,g4) = -1.5708
    c: Tangent(g0,g5) = -1.5708
    c: Tangent(g1,g5) = -1.5708
    c: Tangent(g1,g6) = -1.5708
    c: Tangent(g2,g6) = -1.5708
    c: Tangent(g2,g7) = -1.5708
    c: Tangent(g3,g7) = -1.5708
    c: Tangent(g3,g4) = -1.5708
    c: Horizontal(g0)
    c: Horizontal(g2)
    c: Vertical(g1)
    c: Vertical(g3)
    c: Equal(g4,g5)
    c: Equal(g6,g7)
    c: PointOnObject(g8,g0)
    c: PointOnObject(g8,g3)
    c: PointOnObject(g9,g1)
    c: PointOnObject(g9,g2)
    c: DistanceX(g2) = -13
    c: DistanceX(g2) = -18.1
    c: Radius(g6) = 2
    c: Symmetric(g5,g6,g-1)
    c: DistanceY(g8,g9) = 100
FEATURE [PartDesign::Pocket] Pocket032
  BaseFeature = -> MultiTransform
  Direction = (0,1,-2e-16)
  Length = 5
  Length2 = 5
  Profile = -> Sketch113
  ReferenceAxis = -> Sketch113 [N_Axis]
  Suppressed = false
  Type = 1
FEATURE [PartDesign::LinearPattern] LinearPattern
  BaseFeature = -> Pocket032
  Direction = -> Sketch113 [V_Axis]
  Length = 1078.25
  Mode = 0
  Occurrences = 2
  Offset = 1078.25
  Originals = -> [Pocket032]
  Suppressed = false
  expr: Length = <<bar_pad>>.Length - <<Sketch113>>.AttachmentOffset.Base.y * 2
FEATURE [PartDesign::Body] Body005  label="bar"
  Group = -> [Binder008,Pad008,Boolean004,Local_CS016,Local_CS018,Sketch057,Pocket007,DatumPlane001,MultiTransform,Mirrored003,Mirrored004,Sketch058,Sketch113,Pocket032,LinearPattern]
  Origin = -> Origin006
  Tip = -> LinearPattern
COMPONENT P3 — recipe-attached ("bar_fix", modeled in this document).
Construction recipe (the document's own serialized feature program — sketch geometry with constraints, then the solid features built on it; lengths are millimeters unless a unit is written):

FEATURE [PartDesign::SubShapeBinder] Binder009
  BindCopyOnChange = 0
  BindMode = 0
  ClaimChildren = true
  Context = -> Body006 [Binder009.]
  Fuse = false
  MakeFace = true
  OffsetFill = false
  OffsetIntersection = false
  OffsetJoinType = 0
  OffsetOpenResult = false
  PartialLoad = false
  Placement = pos=(0,0,0) rot=(0.57735,0.57735,0.57735;2.0944rad)
  Relative = false
  Support = -> [Sketch035]
  _Version = 2
FEATURE [PartDesign::FeaturePython] BaseBend002  label="bar_fix_BaseBend"  # WARN: FeaturePython — macro-defined, semantics opaque (R4)
  BendSide = 1
  BendSketch = -> Binder009
  MidPlane = true
  Reverse = false
  Suppressed = false
  length = 26
  radius = 2
  thickness = 0.7
  expr: length = <<bar_base_sketch>>.Constraints.inner_plane_width
FEATURE [PartDesign::CoordinateSystem] Local_CS017  label="bar_fix_orig"
  AttacherType = Attacher::AttachEngine3D
  AttachmentOffset = pos=(0,0,0) rot=(0,0,1;3.14159rad)
  MapMode = 5
  Placement = pos=(0,0,0) rot=(0,0,1;3.14159rad)
FEATURE [Sketcher::SketchObject] Sketch059
  AttachmentOffset = pos=(13,40,0) rot=(0,0,1;0rad)
  FullyConstrained = true
  MapMode = 5
  Placement = pos=(13,8.9e-15,40) rot=(1,0,0;1.5708rad)
  expr: .AttachmentOffset.Base.x = <<bar_fix_BaseBend>>.length / 2
  expr: .AttachmentOffset.Base.y = <<bar_fix_base_sketch>>.Constraints.bar_side
  sketch-geometry (3):
    g0: ArcOfCircle CenterX=-5 CenterY=-5 CenterZ=0 NormalX=0 NormalY=0 NormalZ=1 AngleXU=0 Radius=5 StartAngle=-2.7e-15 EndAngle=1.5708
    g1: LineSegment StartX=-5 StartY=0 StartZ=0 EndX=0 EndY=0 EndZ=0
    g2: LineSegment StartX=0 StartY=0 StartZ=0 EndX=0 EndY=-5 EndZ=0
  constraints (7):
    c: PointOnObject(g0,g-1)
    c: PointOnObject(g0,g-2)
    c: Coincident(g1,g-1)
    c: Coincident(g2,g1)
    c: Tangent(g2,g0) = 1.5708
    c: Tangent(g1,g0) = 1.5708
    c: Radius(g0) = 5
FEATURE [PartDesign::Pocket] Pocket009
  BaseFeature = -> BaseBend002
  Direction = (0,1,-2e-16)
  Length = 5
  Length2 = 5
  Midplane = true
  Profile = -> Sketch059
  ReferenceAxis = -> Sketch059 [N_Axis]
  Suppressed = false
  Type = 1
FEATURE [Sketcher::SketchObject] Sketch060
  AttachmentOffset = pos=(13,50,0) rot=(0,0,1;0rad)
  FullyConstrained = true
  MapMode = 5
  Placement = pos=(13,50,0) rot=(0,0,1;0rad)
  expr: .AttachmentOffset.Base.x = <<bar_fix_BaseBend>>.length / 2
  expr: .AttachmentOffset.Base.y = <<bar_fix_base_sketch>>.Constraints.comp_side
  sketch-geometry (3):
    g0: LineSegment StartX=-5 StartY=0 StartZ=0 EndX=0 EndY=0 EndZ=0
    g1: LineSegment StartX=0 StartY=0 StartZ=0 EndX=0 EndY=-5 EndZ=0
    g2: ArcOfCircle CenterX=-5 CenterY=-5 CenterZ=0 NormalX=0 NormalY=0 NormalZ=1 AngleXU=0 Radius=5 StartAngle=0 EndAngle=1.5708
  constraints (7):
    c: PointOnObject(g0,g-1)
    c: Coincident(g0,g-1)
    c: Coincident(g0,g1)
    c: PointOnObject(g1,g-2)
    c: Tangent(g2,g0) = 1.5708
    c: Tangent(g2,g1) = 1.5708
    c: Radius(g2) = 5
FEATURE [PartDesign::Pocket] Pocket010
  BaseFeature = -> Pocket009
  Direction = (0,0,-1)
  Length = 5
  Length2 = 5
  Midplane = true
  Profile = -> Sketch060
  ReferenceAxis = -> Sketch060 [N_Axis]
  Suppressed = false
  Type = 1
FEATURE [PartDesign::Mirrored] Mirrored005
  BaseFeature = -> Pocket010
  MirrorPlane = -> YZ_Plane007
  Originals = -> [Pocket009,Pocket010]
  Suppressed = false
FEATURE [PartDesign::Boolean] Boolean005
  BaseFeature = -> Mirrored005
  Group = -> [Compound013]
  Suppressed = false
  Type = 1
  UsePlacement = true
FEATURE [PartDesign::Body] Body006  label="bar_fix"
  Group = -> [Binder009,BaseBend002,Sketch059,Pocket009,Sketch060,Pocket010,Mirrored005,Boolean005,Local_CS017]
  Origin = -> Origin007
  Tip = -> Boolean005
COMPONENT P4 — recipe-attached ("sink_back", modeled in this document).
Construction recipe (the document's own serialized feature program — sketch geometry with constraints, then the solid features built on it; lengths are millimeters unless a unit is written):

FEATURE [PartDesign::CoordinateSystem] Local_CS020
  AttacherType = Attacher::AttachEngine3D
  AttachmentOffset = pos=(0,3,0) rot=(0,0,1;0rad)
  AttachmentSupport = -> [XY_Plane008]
  MapMode = 5
  Placement = pos=(0,3,0) rot=(0,0,1;0rad)
FEATURE [PartDesign::SubShapeBinder] Binder010
  BindCopyOnChange = 0
  BindMode = 0
  ClaimChildren = true
  Context = -> Body007 [Binder010.]
  Fuse = false
  MakeFace = true
  OffsetFill = false
  OffsetIntersection = false
  OffsetJoinType = 0
  OffsetOpenResult = false
  PartialLoad = false
  Placement = pos=(0,0,0) rot=(1,0,0;1.5708rad)
  Relative = false
  Support = -> [Sketch040]
  _Version = 2
FEATURE [Sketcher::SketchObject] Sketch042  label="sink_back_base_Sketch"
  ExternalGeometry = -> [Binder010]
  FullyConstrained = false
  MapMode = 5
  Placement = pos=(0,0,0) rot=(0.57735,0.57735,0.57735;2.0944rad)
  sketch-geometry (11):
    g0: LineSegment StartX=0 StartY=-33.9589 StartZ=0 EndX=7.8e-15 EndY=35 EndZ=0
    g1: LineSegment StartX=7.8e-15 StartY=35 StartZ=0 EndX=-0.5 EndY=35 EndZ=0
    g2: LineSegment StartX=-0.5 StartY=35 StartZ=0 EndX=-0.5 EndY=-33.9589 EndZ=0
    g3: LineSegment StartX=0.566059 StartY=-36.0067 StartZ=0 EndX=3.27471 EndY=-37.9034 EndZ=0
    g4: LineSegment StartX=3.27471 StartY=-37.9034 StartZ=0 EndX=3.5615 EndY=-37.4938 EndZ=0
    g5: LineSegment StartX=3.5615 StartY=-37.4938 StartZ=0 EndX=0.852847 EndY=-35.5972 EndZ=0
    g6: ArcOfCircle CenterX=2 CenterY=-33.9589 CenterZ=0 NormalX=0 NormalY=0 NormalZ=1 AngleXU=0 Radius=2 StartAngle=3.14159 EndAngle=4.10152
    g7: GeomPoint X=0 Y=-35 Z=0
    g8: ArcOfCircle CenterX=2 CenterY=-33.9589 CenterZ=0 NormalX=0 NormalY=0 NormalZ=1 AngleXU=0 Radius=2.5 StartAngle=3.14159 EndAngle=4.10152
    g9: GeomPoint X=-0.5 Y=-35.2603 Z=0
    g10: LineSegment StartX=0.566059 StartY=-36.0067 StartZ=0 EndX=0.852847 EndY=-35.5972 EndZ=0
  constraints (26):
    c: PointOnObject(g7,g-2)
    c: Coincident(g0,g1)
    c: Horizontal(g1)
    c: Coincident(g1,g2)
    c: Vertical(g2)
    c: Coincident(g3,g4)
    c: Coincident(g4,g5)
    c: PointOnObject(g7,g0)
    c: PointOnObject(g7,g5)
    c: Tangent(g0,g6) = 1.5708
    c: Tangent(g5,g6) = 1.5708
    c: PointOnObject(g9,g2)
    c: PointOnObject(g9,g3)
    c: Tangent(g2,g8) = -1.5708
    c: Tangent(g3,g8) = -1.5708
    c: Coincident(g8,g6)
    c: DistanceX(g1,g1) = 0.5
    c: Perpendicular(g5,g4)
    c: Perpendicular(g3,g4)
    c: Radius(g6) = 2
    c: Angle(g5) = 2.53073
    c: Coincident(g10,g8)
    c: Angle(g5,g-1) = 0.610865  'angle'
    c: Coincident(g10,g6)
    c: Coincident(g0,g-4)
    c: PointOnObject(g-3,g5)
FEATURE [Sketcher::SketchObject] Sketch041
  AttachmentOffset = pos=(0,0,-35) rot=(1,0,0;-0.610865rad)
  AttachmentSupport = -> [XY_Plane008]
  ExternalGeometry = -> [Sketch042,Binder010]
  FullyConstrained = true
  MapMode = 5
  Placement = pos=(0,0,-35) rot=(1,0,0;5.67232rad)
  expr: .AttachmentOffset.Rotation.Angle = -<<sink_back_base_Sketch>>.Constraints.angle
  sketch-geometry (4):
    g0: LineSegment StartX=-309.563 StartY=1.04113 StartZ=0 EndX=204.635 EndY=1.04113 EndZ=0
    g1: LineSegment StartX=204.635 StartY=1.04113 StartZ=0 EndX=204.635 EndY=26.0411 EndZ=0
    g2: LineSegment StartX=204.635 StartY=26.0411 StartZ=0 EndX=-309.563 EndY=66.0411 EndZ=0
    g3: LineSegment StartX=-309.563 StartY=66.0411 StartZ=0 EndX=-309.563 EndY=1.04113 EndZ=0
  constraints (13):
    c: Coincident(g0,g1)
    c: Coincident(g1,g2)
    c: Coincident(g2,g3)
    c: Horizontal(g0)
    c: Vertical(g1)
    c: Vertical(g3)
    c: Coincident(g0,g3)
    c: PointOnObject(g-3,g0)
    c: PointOnObject(g-4,g1)
    c: PointOnObject(g-5,g3)
    c: DistanceY(g1,g2) = 40
    c: DistanceY(g1,g1) = 25
    c: Distance(g2) = 515.751  'end'
FEATURE [Sketcher::SketchObject] Sketch043
  AttachmentSupport = -> [Sketch041]
  ExternalGeometry = -> [Sketch041]
  FullyConstrained = true
  MapMode = 7
  Placement = pos=(204.635,21.3316,-49.9366) rot=(0.593097,0.556507,0.581839;2.03146rad)
  sketch-geometry (6):
    g0: LineSegment StartX=2e-16 StartY=-8.9e-15 StartZ=0 EndX=-0.286208 EndY=-0.409982 EndZ=0
    g1: ArcOfCircle CenterX=1.14483 CenterY=1.63993 CenterZ=0 NormalX=0 NormalY=0 NormalZ=1 AngleXU=0 Radius=2 StartAngle=4.10294 EndAngle=5.67374
    g2: ArcOfCircle CenterX=1.14483 CenterY=1.63993 CenterZ=0 NormalX=0 NormalY=0 NormalZ=1 AngleXU=0 Radius=2.5 StartAngle=4.10294 EndAngle=5.67374
    g3: LineSegment StartX=2.78476 StartY=0.495097 StartZ=0 EndX=16.4011 EndY=20 EndZ=0
    g4: LineSegment StartX=16.4011 StartY=20 StartZ=0 EndX=16.8111 EndY=19.7138 EndZ=0
    g5: LineSegment StartX=16.8111 StartY=19.7138 StartZ=0 EndX=3.19474 EndY=0.208889 EndZ=0
  constraints (16):
    c: Coincident(g0,g-3)
    c: Coincident(g1,g0)
    c: Coincident(g2,g1)
    c: Coincident(g2,g0)
    c: Tangent(g1,g3) = -1.5708
    c: Coincident(g3,g4)
    c: Coincident(g4,g5)
    c: Perpendicular(g-3,g0)
    c: Perpendicular(g1,g0)
    c: Tangent(g5,g2) = 1.5708
    c: Distance(g0) = 0.5
    c: Perpendicular(g3,g4)
    c: Perpendicular(g5,g4)
    c: Angle(g3,g-3) = 1.5708
    c: Radius(g1) = 2
    c: DistanceY(g3) = 20
FEATURE [PartDesign::Pad] Pad009  label="sink_back_base_Pad009"
  Direction = (1,0,0)
  Length = 204.635
  Length2 = 309.563
  Placement = pos=(0,0,0) rot=(0.57735,0.57735,0.57735;2.0944rad)
  Profile = -> Sketch042
  ReferenceAxis = -> Sketch042 [N_Axis]
  Suppressed = false
  Type = 4
  expr: Length = <<sink_front_sketch>>.Constraints.right
  expr: Length2 = <<sink_front_sketch>>.Constraints.left
FEATURE [PartDesign::Pad] Pad010
  BaseFeature = -> Pad009
  Direction = (0,0.573576,0.819152)
  Length = 0.5
  Length2 = 10
  Placement = pos=(0,0,0) rot=(0.57735,0.57735,0.57735;2.0944rad)
  Profile = -> Sketch041
  ReferenceAxis = -> Sketch041 [N_Axis]
  Reversed = true
  Suppressed = false
  Type = 0
FEATURE [Sketcher::SketchObject] Sketch061
  AttachmentSupport = -> [XZ_Plane008]
  ExternalGeometry = -> [Sketch042]
  FullyConstrained = true
  MapMode = 5
  Placement = pos=(0,0,0) rot=(1,0,0;1.5708rad)
  expr: Constraints[14] = <<sink_back_base_Pad009>>.Length
  expr: Constraints[15] = -<<sink_back_base_Pad009>>.Length2
  sketch-geometry (6):
    g0: LineSegment StartX=204.635 StartY=30 StartZ=0 EndX=204.635 EndY=35 EndZ=0
    g1: LineSegment StartX=204.635 StartY=35 StartZ=0 EndX=199.635 EndY=35 EndZ=0
    g2: LineSegment StartX=-304.563 StartY=35 StartZ=0 EndX=-309.563 EndY=35 EndZ=0
    g3: LineSegment StartX=-309.563 StartY=35 StartZ=0 EndX=-309.563 EndY=30 EndZ=0
    g4: ArcOfCircle CenterX=199.635 CenterY=30 CenterZ=0 NormalX=0 NormalY=0 NormalZ=1 AngleXU=0 Radius=5 StartAngle=-1.35e-13 EndAngle=1.5708
    g5: ArcOfCircle CenterX=-304.563 CenterY=30 CenterZ=0 NormalX=0 NormalY=0 NormalZ=1 AngleXU=0 Radius=5 StartAngle=1.5708 EndAngle=3.14159
  constraints (16):
    c: Vertical(g0)
    c: Coincident(g0,g1)
    c: Horizontal(g1)
    c: Coincident(g2,g3)
    c: Vertical(g3)
    c: Horizontal(g2)
    c: Horizontal(g2,g0)
    c: Tangent(g5,g2) = -1.5708
    c: Tangent(g5,g3) = -1.5708
    c: Radius(g5) = 5
    c: Tangent(g4,g0) = -1.5708
    c: Tangent(g4,g1) = -1.5708
    c: Equal(g4,g5)
    c: Horizontal(g-3,g0)
    c: DistanceX(g0) = 204.635
    c: DistanceX(g2) = -309.563
FEATURE [Sketcher::SketchObject] Sketch062
  AttachmentSupport = -> [Sketch043]
  FullyConstrained = true
  MapMode = 51
  Placement = pos=(204.79,37.7561,-29.9564) rot=(0.999043,-0.020198,0.0388;4.10074rad)
  expr: Constraints[8] = -<<Pad011>>.Length
  sketch-geometry (6):
    g0: LineSegment StartX=0 StartY=5 StartZ=0 EndX=0 EndY=0 EndZ=0
    g1: LineSegment StartX=0 StartY=0 StartZ=0 EndX=-5 EndY=0 EndZ=0
    g2: LineSegment StartX=-515.751 StartY=5 StartZ=0 EndX=-515.751 EndY=0 EndZ=0
    g3: LineSegment StartX=-515.751 StartY=0 StartZ=0 EndX=-510.751 EndY=0 EndZ=0
    g4: ArcOfCircle CenterX=-5 CenterY=5 CenterZ=0 NormalX=0 NormalY=0 NormalZ=1 AngleXU=0 Radius=5 StartAngle=4.71239 EndAngle=6.28319
    g5: ArcOfCircle CenterX=-510.751 CenterY=5 CenterZ=0 NormalX=0 NormalY=0 NormalZ=1 AngleXU=0 Radius=5 StartAngle=3.14159 EndAngle=4.71239
  constraints (15):
    c: PointOnObject(g0,g-2)
    c: Coincident(g0,g-1)
    c: Coincident(g0,g1)
    c: PointOnObject(g1,g-1)
    c: Vertical(g2)
    c: Coincident(g2,g3)
    c: PointOnObject(g3,g-1)
    c: Horizontal(g3)
    c: DistanceX(g2) = -515.751
    c: Tangent(g4,g0) = 1.5708
    c: Tangent(g4,g1) = 1.5708
    c: Tangent(g5,g3) = -1.5708
    c: Tangent(g5,g2) = -1.5708
    c: Equal(g4,g5)
    c: Radius(g4) = 5
FEATURE [Sketcher::SketchObject] Sketch063
  AttachmentSupport = -> [XZ_Plane008]
  ExternalGeometry = -> [Binder010]
  FullyConstrained = true
  MapMode = 5
  Placement = pos=(0,0,0) rot=(1,0,0;1.5708rad)
  expr: Constraints[1] = -<<Dimensions>>.Constraints.modules_face / 2
  sketch-geometry (10):
    g0: GeomPoint X=-164.635 Y=0 Z=0
    g1: LineSegment StartX=-309.563 StartY=35 StartZ=0 EndX=-309.563 EndY=4.5 EndZ=0
    g2: LineSegment StartX=-307.063 StartY=7 StartZ=0 EndX=-167.135 EndY=7 EndZ=0
    g3: LineSegment StartX=-164.635 StartY=9.5 StartZ=0 EndX=-164.635 EndY=32.5 EndZ=0
    g4: LineSegment StartX=-162.135 StartY=35 StartZ=0 EndX=-309.563 EndY=35 EndZ=0
    g5: ArcOfCircle CenterX=-307.063 CenterY=4.5 CenterZ=0 NormalX=0 NormalY=0 NormalZ=1 AngleXU=0 Radius=2.5 StartAngle=1.5708 EndAngle=3.14159
    g6: ArcOfCircle CenterX=-167.135 CenterY=9.5 CenterZ=0 NormalX=0 NormalY=0 NormalZ=1 AngleXU=0 Radius=2.5 StartAngle=4.71239 EndAngle=6.28319
    g7: ArcOfCircle CenterX=-162.135 CenterY=32.5 CenterZ=0 NormalX=0 NormalY=0 NormalZ=1 AngleXU=0 Radius=2.5 StartAngle=1.5708 EndAngle=3.14159
    g8: GeomPoint X=-309.563 Y=35 Z=0
    g9: GeomPoint X=-164.635 Y=7 Z=0
  constraints (22):
    c: PointOnObject(g0,g-1)
    c: DistanceX(g0) = -164.635
    c: Tangent(g2,g6) = -1.5708
    c: Tangent(g3,g6) = -1.5708
    c: Vertical(g1)
    c: Vertical(g3)
    c: Horizontal(g2)
    c: Horizontal(g4)
    c: Equal(g5,g6)
    c: Equal(g6,g7)
    c: PointOnObject(g9,g2)
    c: PointOnObject(g9,g3)
    c: Diameter(g6) = 5
    c: Vertical(g9,g0)
    c: DistanceY(g0,g9) = 7
    c: Tangent(g7,g3) = 1.5708
    c: Tangent(g4,g7) = -1.5708
    c: Tangent(g5,g2) = 1.5708
    c: Tangent(g5,g1) = -1.5708
    c: Coincident(g8,g-3)
    c: Coincident(g1,g8)
    c: Coincident(g1,g4)
FEATURE [PartDesign::FeaturePython] Bend016  # WARN: FeaturePython — macro-defined, semantics opaque (R4)
  AutoMiter = false
  BaseFeature = -> Pad010
  BendType = 0
  LengthList = [26]
  LengthSpec = 0
  ReliefFactor = 0.7
  Suppressed = false
  UseReliefFactor = false
  angle = 90
  baseObject = -> Pad010 [Edge25]
  bendAList = [90]
  extend1 = 2
  extend2 = 2
  gap1 = 0
  gap2 = 0
  invert = true
  kfactor = 0.5
  length = 26
  maxExtendDist = 5
  minGap = 0.2
  minReliefGap = 1
  miterangle1 = -35
  miterangle2 = 0
  offset = 0
  radius = 1
  reliefType = 0
  reliefd = 1
  reliefw = 0.8
  sketchflip = false
  sketchinvert = false
  unfold = false
  expr: miterangle1 = -<<sink_back_base_Sketch>>.Constraints.angle
FEATURE [Sketcher::SketchObject] Sketch114
  AttachmentOffset = pos=(0,0,205) rot=(0,0,1;0rad)
  AttachmentSupport = -> [YZ_Plane008]
  ExternalGeometry = -> [Sketch043]
  FullyConstrained = true
  MapMode = 5
  Placement = pos=(205,0,0) rot=(0.57735,0.57735,0.57735;2.0944rad)
  expr: Constraints[23] = 90 deg - <<sink_back_base_Sketch>>.Constraints.angle
  sketch-geometry (10):
    g0: LineSegment StartX=-1 StartY=0 StartZ=0 EndX=-1 EndY=-30 EndZ=0
    g1: LineSegment StartX=38.7813 StartY=-30 StartZ=0 EndX=38.7813 EndY=0 EndZ=0
    g2: LineSegment StartX=38.7813 StartY=0 StartZ=0 EndX=-1 EndY=0 EndZ=0
    g3: LineSegment StartX=-1 StartY=-30 StartZ=0 EndX=-0.5 EndY=-30 EndZ=0
    g4: LineSegment StartX=37.7813 StartY=-30 StartZ=0 EndX=38.7813 EndY=-30 EndZ=0
    g5: LineSegment StartX=-0.5 StartY=-30 StartZ=0 EndX=-0.5 EndY=-32 EndZ=0
    g6: LineSegment StartX=1.5 StartY=-30 StartZ=0 EndX=33.9394 EndY=-30 EndZ=0
    g7: LineSegment StartX=35.5777 StartY=-33.1472 StartZ=0 EndX=37.7813 EndY=-30 EndZ=0
    g8: ArcOfCircle CenterX=1.5 CenterY=-32 CenterZ=0 NormalX=0 NormalY=0 NormalZ=1 AngleXU=0 Radius=2 StartAngle=1.5708 EndAngle=3.14159
    g9: ArcOfCircle CenterX=33.9394 CenterY=-32 CenterZ=0 NormalX=0 NormalY=0 NormalZ=1 AngleXU=0 Radius=2 StartAngle=5.67232 EndAngle=7.85398
  constraints (30):
    c: Coincident(g0,g3)
    c: Coincident(g4,g1)
    c: Coincident(g1,g2)
    c: Coincident(g2,g0)
    c: Vertical(g0)
    c: Vertical(g1)
    c: Horizontal(g2)
    c: PointOnObject(g0,g-1)
    c: DistanceX(g0) = -1
    c: DistanceY(g4) = -30
    c: DistanceX(g1) = 38.7813
    c: Coincident(g3,g5)
    c: Horizontal(g3)
    c: Coincident(g7,g4)
    c: Horizontal(g4)
    c: Horizontal(g6)
    c: Horizontal(g0,g6)
    c: Vertical(g5)
    c: Tangent(g8,g5) = -1.5708
    c: Tangent(g8,g6) = 1.5708
    c: DistanceX(g3) = -0.5
    c: Tangent(g9,g6) = 1.5708
    c: Tangent(g9,g7) = -1.5708
    c: Angle(g7) = 0.959931
    c: Equal(g9,g8)
    c: Radius(g9) = 2
    c: Horizontal(g6,g1)
    c: DistanceX(g4) = 37.7813
    c: DistanceX(g4,g4) = 1
    c: DistanceX(g-3,g4) = 0.0252
FEATURE [PartDesign::Pocket] Pocket033
  BaseFeature = -> Bend016
  Direction = (-1,0,0)
  Length = 5
  Length2 = 5
  Profile = -> Sketch114
  ReferenceAxis = -> Sketch114 [N_Axis]
  Reversed = true
  Suppressed = false
  Type = 0
FEATURE [PartDesign::Pad] Pad011
  BaseFeature = -> Pocket033
  Direction = (0.996988,-0.0635308,0.0444847)
  Length = 515.751
  Length2 = 10
  Profile = -> Sketch043
  ReferenceAxis = -> Sketch043 [N_Axis]
  Reversed = true
  Suppressed = false
  Type = 0
  expr: Length = Sketch041.Constraints.end
FEATURE [PartDesign::Pocket] Pocket011
  BaseFeature = -> Pad011
  Direction = (0,1,-2e-16)
  Length = 5
  Length2 = 5
  Midplane = true
  Profile = -> Sketch061
  ReferenceAxis = -> Sketch061 [N_Axis]
  Suppressed = false
  Type = 1
FEATURE [PartDesign::Pocket] Pocket012
  BaseFeature = -> Pocket011
  Direction = (-0.0775567,-0.816685,0.571849)
  Length = 5
  Length2 = 5
  Profile = -> Sketch062
  ReferenceAxis = -> Sketch062 [N_Axis]
  Reversed = true
  Suppressed = false
  Type = 1
FEATURE [PartDesign::Pocket] Pocket013
  BaseFeature = -> Pocket012
  Direction = (0,1,-2e-16)
  Length = 5
  Length2 = 5
  Midplane = true
  Profile = -> Sketch063
  ReferenceAxis = -> Sketch063 [N_Axis]
  Suppressed = false
  Type = 1
FEATURE [PartDesign::Boolean] Boolean007
  BaseFeature = -> Pocket013
  Group = -> [Compound015]
  Suppressed = false
  Type = 1
  UsePlacement = true
FEATURE [PartDesign::Body] Body007  label="sink_back"
  Group = -> [Local_CS020,Binder010,Sketch041,Sketch042,Sketch043,Pad009,Pad010,Bend016,Sketch114,Pocket033,Pad011,Sketch061,Pocket011,Sketch062,Pocket012,Sketch063,Pocket013,Boolean007]
  Origin = -> Origin008
  Tip = -> Boolean007
COMPONENT P5 — recipe-attached ("door_fix1", modeled in this document).
Construction recipe (the document's own serialized feature program — sketch geometry with constraints, then the solid features built on it; lengths are millimeters unless a unit is written):

FEATURE [PartDesign::SubShapeBinder] Binder015
  BindCopyOnChange = 0
  BindMode = 0
  ClaimChildren = false
  Context = -> Body009 [Binder015.]
  Fuse = false
  MakeFace = true
  OffsetFill = false
  OffsetIntersection = false
  OffsetJoinType = 0
  OffsetOpenResult = false
  PartialLoad = false
  Relative = true
  Support = -> [Sketch046]
  _Version = 2
FEATURE [Sketcher::SketchObject] Sketch050
  AttachmentOffset = pos=(0,0,-13) rot=(0,0,1;0rad)
  ExternalGeometry = -> [Binder015]
  FullyConstrained = true
  MapMode = 5
  Placement = pos=(0,0,-13) rot=(0,0,1;0rad)
  sketch-geometry (4):
    g0: LineSegment StartX=-15 StartY=-1.8e-15 StartZ=0 EndX=15 EndY=3.091e-13 EndZ=0
    g1: ArcOfCircle CenterX=10 CenterY=23.1324 CenterZ=0 NormalX=0 NormalY=0 NormalZ=1 AngleXU=0 Radius=7 StartAngle=0.0322243 EndAngle=2.14272
    g2: ArcOfCircle CenterX=33.2738 CenterY=-13.0246 CenterZ=0 NormalX=0 NormalY=0 NormalZ=1 AngleXU=0 Radius=50 StartAngle=2.14272 EndAngle=2.87806
    g3: ArcOfCircle CenterX=-82.9517 CenterY=20.1361 CenterZ=0 NormalX=0 NormalY=0 NormalZ=1 AngleXU=0 Radius=100 StartAngle=6.08044 EndAngle=6.31541
  constraints (11):
    c: PointOnObject(g0,g-1)
    c: Symmetric(g0,g0,g-2)
    c: Coincident(g1,g-3)
    c: Coincident(g2,g0)
    c: Coincident(g3,g0)
    c: Tangent(g2,g1) = -1.5708
    c: Tangent(g3,g1) = -1.5708
    c: DistanceX(g0,g0) = 30
    c: Radius(g1) = 7
    c: Radius(g2) = 50
    c: Radius(g3) = 100
FEATURE [Sketcher::SketchObject] Sketch051
  AttachmentOffset = pos=(0,0,-7) rot=(0,0,1;0rad)
  ExternalGeometry = -> [Sketch050]
  FullyConstrained = true
  MapMode = 5
  Placement = pos=(0,0,-7) rot=(0,0,1;0rad)
  sketch-geometry (4):
    g0: ArcOfCircle CenterX=33.2738 CenterY=-13.0246 CenterZ=0 NormalX=0 NormalY=0 NormalZ=1 AngleXU=0 Radius=50 StartAngle=2.61743 EndAngle=2.87806
    g1: ArcOfCircle CenterX=-82.9517 CenterY=20.1361 CenterZ=0 NormalX=0 NormalY=0 NormalZ=1 AngleXU=0 Radius=100 StartAngle=6.08044 EndAngle=6.20173
    g2: LineSegment StartX=-10.0132 StartY=12 StartZ=0 EndX=16.7168 EndY=12 EndZ=0
    g3: LineSegment StartX=-15 StartY=-1.8e-15 StartZ=0 EndX=15 EndY=1.5419e-12 EndZ=0
  constraints (10):
    c: Coincident(g0,g-4)
    c: Coincident(g0,g-4)
    c: Coincident(g1,g-3)
    c: Coincident(g1,g-3)
    c: Coincident(g2,g0)
    c: Coincident(g2,g1)
    c: Horizontal(g2)
    c: DistanceY(g1) = 12
    c: Coincident(g3,g0)
    c: Coincident(g3,g1)
FEATURE [PartDesign::Pad] Pad013
  Direction = (0,0,1)
  Length = 6
  Length2 = 10
  Profile = -> Sketch050
  ReferenceAxis = -> Sketch050 [N_Axis]
  Suppressed = false
  Type = 0
  expr: Length = <<Sketch051>>.AttachmentOffset.Base.z - <<Sketch050>>.AttachmentOffset.Base.z
FEATURE [PartDesign::Pad] Pad014
  BaseFeature = -> Pad013
  Direction = (0,0,1)
  Length = 7
  Length2 = 10
  Profile = -> Sketch051
  ReferenceAxis = -> Sketch051 [N_Axis]
  Suppressed = false
  Type = 0
  expr: Length = -<<Sketch051>>.AttachmentOffset.Base.z
FEATURE [PartDesign::Plane] DatumPlane
  AttachmentOffset = pos=(0,0,7) rot=(0,0,1;0rad)
  Length = 60.4972
  MapMode = 5
  Placement = pos=(0,0,7) rot=(0,0,1;0rad)
  ResizeMode = 0
  Width = 65.5925
  expr: .AttachmentOffset.Base.z = <<Pad014>>.Length
FEATURE [PartDesign::Mirrored] Mirrored001
  BaseFeature = -> Pad014
  MirrorPlane = -> XY_Plane011
  Originals = -> [Pad014,Pad013]
  Suppressed = false
FEATURE [PartDesign::Pocket] Pocket005
  BaseFeature = -> Mirrored001
  Direction = (0,0,-1)
  Length = 5
  Length2 = 5
  Midplane = true
  Profile = -> Binder015
  Refine = true
  Suppressed = false
  Type = 1
FEATURE [PartDesign::CoordinateSystem] Local_CS022  label="door_rot_axis"
  AttacherType = Attacher::AttachEngine3D
  MapMode = 45
  Placement = pos=(10,23.1324,0) rot=(0,0,1;1.2e-05rad)
FEATURE [PartDesign::Boolean] Boolean009
  BaseFeature = -> Pocket005
  Group = -> [Compound017]
  Suppressed = false
  Type = 1
  UsePlacement = true
FEATURE [PartDesign::CoordinateSystem] Local_CS023  label="door_fix"
  AttacherType = Attacher::AttachEngine3D
  AttachmentOffset = pos=(0,0,0) rot=(0,1,0;3.14159rad)
  MapMode = 5
  Placement = pos=(0,0,0) rot=(0,0.707107,0.707107;3.14159rad)
FEATURE [PartDesign::Body] Body009  label="door_fix1"
  Group = -> [Sketch050,Binder015,Sketch051,Pad013,Pad014,DatumPlane,Mirrored001,Pocket005,Local_CS022,Boolean009,Local_CS023]
  Origin = -> Origin011
  Tip = -> Boolean009
COMPONENT P6 — recipe-attached ("door_fix2", modeled in this document).
Construction recipe (the document's own serialized feature program — sketch geometry with constraints, then the solid features built on it; lengths are millimeters unless a unit is written):

FEATURE [PartDesign::SubShapeBinder] Binder013
  BindCopyOnChange = 0
  BindMode = 0
  ClaimChildren = true
  Context = -> Body010 [Binder013.]
  Fuse = false
  MakeFace = true
  OffsetFill = false
  OffsetIntersection = false
  OffsetJoinType = 0
  OffsetOpenResult = false
  PartialLoad = false
  Relative = false
  Support = -> [Sketch048]
  _Version = 2
FEATURE [PartDesign::Pad] Pad012
  Direction = (0,0,1)
  Length = 13
  Length2 = 10
  Midplane = true
  Profile = -> Binder013
  Suppressed = false
  Type = 0
FEATURE [PartDesign::SubShapeBinder] Binder014
  BindCopyOnChange = 0
  BindMode = 0
  ClaimChildren = false
  Context = -> Body010 [Binder014.]
  Fuse = false
  MakeFace = true
  OffsetFill = false
  OffsetIntersection = false
  OffsetJoinType = 0
  OffsetOpenResult = false
  PartialLoad = false
  Relative = true
  Support = -> [Sketch049]
  _Version = 2
FEATURE [PartDesign::Pocket] Pocket004
  BaseFeature = -> Pad012
  Direction = (0,0,-1)
  Length = 5
  Length2 = 5
  Midplane = true
  Profile = -> Binder014
  Suppressed = false
  Type = 1
FEATURE [PartDesign::CoordinateSystem] Local_CS021  label="door_rot_axis2"
  AttacherType = Attacher::AttachEngine3D
  MapMode = 45
  Placement = pos=(8e-15,4.74044,0) rot=(0,0,1.16318;0rad)
FEATURE [PartDesign::Body] Body010  label="door_fix2"
  Group = -> [Binder013,Pad012,Binder014,Pocket004,Local_CS021]
  Origin = -> Origin012
  Tip = -> Pocket004
COMPONENT P7 — recipe-attached ("Body011", modeled in this document).
Construction recipe (the document's own serialized feature program — sketch geometry with constraints, then the solid features built on it; lengths are millimeters unless a unit is written):

FEATURE [Sketcher::SketchObject] Sketch052
  FullyConstrained = true
  MapMode = 5
  sketch-geometry (1):
    g0: Circle CenterX=0 CenterY=0 CenterZ=0 NormalX=0 NormalY=0 NormalZ=1 AngleXU=0 Radius=3.025
  constraints (2):
    c: Coincident(g0,g-1)
    c: Diameter(g0) = 6.05
FEATURE [Sketcher::SketchObject] Sketch053
  FullyConstrained = true
  MapMode = 5
  sketch-geometry (1):
    g0: Circle CenterX=0 CenterY=0 CenterZ=0 NormalX=0 NormalY=0 NormalZ=1 AngleXU=0 Radius=1.75
  constraints (2):
    c: Coincident(g0,g-1)
    c: Diameter(g0) = 3.5
FEATURE [PartDesign::Pad] Pad015
  Direction = (0,0,1)
  Length = 2.1
  Length2 = 10
  Profile = -> Sketch052
  ReferenceAxis = -> Sketch052 [N_Axis]
  Suppressed = false
  Type = 0
FEATURE [PartDesign::Pad] Pad016
  BaseFeature = -> Pad015
  Direction = (0,0,1)
  Length = 50
  Length2 = 10
  Profile = -> Sketch053
  ReferenceAxis = -> Sketch053 [N_Axis]
  Suppressed = false
  Type = 0
FEATURE [PartDesign::Body] Body011
  Group = -> [Sketch052,Sketch053,Pad015,Pad016]
  Origin = -> Origin013
  Tip = -> Pad016
COMPONENT P8 — recipe-attached ("lamp_fix", modeled in this document).
Construction recipe (the document's own serialized feature program — sketch geometry with constraints, then the solid features built on it; lengths are millimeters unless a unit is written):

FEATURE [PartDesign::SubShapeBinder] Binder016
  BindCopyOnChange = 0
  BindMode = 0
  ClaimChildren = true
  Context = -> Body012 [Binder016.]
  Fuse = false
  MakeFace = true
  OffsetFill = false
  OffsetIntersection = false
  OffsetJoinType = 0
  OffsetOpenResult = false
  PartialLoad = false
  Relative = false
  Support = -> [Sketch064]
  _Version = 2
FEATURE [PartDesign::FeaturePython] BaseBend004  label="lamp_fix_BaseBend"  # WARN: FeaturePython — macro-defined, semantics opaque (R4)
  BendSide = 0
  BendSketch = -> Binder016
  MidPlane = false
  Reverse = false
  Suppressed = false
  length = 900
  radius = 2
  thickness = 0.7
FEATURE [Sketcher::SketchObject] Sketch065  label="lamp_fix_cut_sketch"
  AttachmentOffset = pos=(0,166.7,0) rot=(0,1,0;1.5708rad)
  FullyConstrained = true
  MapMode = 7
  Placement = pos=(318.563,150.075,166.7) rot=(0.313146,0.671543,0.671543;2.53465rad)
  expr: .AttachmentOffset.Base.y = 60 mm + .Constraints.length / 2
  sketch-geometry (8):
    g0: LineSegment StartX=-0.5 StartY=-106.7 StartZ=0 EndX=2.2 EndY=-106.7 EndZ=0
    g1: LineSegment StartX=4.2 StartY=-104.7 StartZ=0 EndX=4.2 EndY=104.7 EndZ=0
    g2: LineSegment StartX=2.2 StartY=106.7 StartZ=0 EndX=-0.5 EndY=106.7 EndZ=0
    g3: LineSegment StartX=-0.5 StartY=106.7 StartZ=0 EndX=-0.5 EndY=-106.7 EndZ=0
    g4: ArcOfCircle CenterX=2.2 CenterY=104.7 CenterZ=0 NormalX=0 NormalY=0 NormalZ=1 AngleXU=0 Radius=2 StartAngle=-2.7e-15 EndAngle=1.5708
    g5: GeomPoint X=4.2 Y=106.7 Z=0
    g6: ArcOfCircle CenterX=2.2 CenterY=-104.7 CenterZ=0 NormalX=0 NormalY=0 NormalZ=1 AngleXU=0 Radius=2 StartAngle=4.71239 EndAngle=6.28319
    g7: GeomPoint X=4.2 Y=-106.7 Z=0
  constraints (19):
    c: Coincident(g2,g3)
    c: Horizontal(g0)
    c: Horizontal(g2)
    c: Vertical(g1)
    c: PointOnObject(g5,g1)
    c: PointOnObject(g5,g2)
    c: Tangent(g1,g4) = -1.5708
    c: Tangent(g2,g4) = -1.5708
    c: Tangent(g0,g6) = -1.5708
    c: Tangent(g1,g6) = -1.5708
    c: Equal(g6,g4)
    c: Radius(g6) = 2  'r'
    c: Coincident(g0,g3)
    c: DistanceX(g0) = -0.5
    c: PointOnObject(g7,g1)
    c: PointOnObject(g7,g0)
    c: Symmetric(g0,g2,g-1)
    c: DistanceY(g3,g3) = 213.4  'length'
    c: DistanceX(g0,g0) = 2.7
FEATURE [Sketcher::SketchObject] Sketch066  label="lamp_fix_cut_sketch2"
  AttachmentOffset = pos=(0,166.7,0) rot=(0,1,0;1.5708rad)
  FullyConstrained = true
  MapMode = 7
  Placement = pos=(299.412,134.005,166.7) rot=(0.889126,0.323616,0.323616;1.68804rad)
  expr: .AttachmentOffset.Base.y = <<lamp_fix_cut_sketch>>.AttachmentOffset.Base.y
  expr: Constraints[6] = <<lamp_fix_cut_sketch>>.Constraints.length
  expr: Constraints[7] = <<lamp_fix_cut_sketch>>.Constraints.r
  sketch-geometry (4):
    g0: ArcOfCircle CenterX=2 CenterY=108.7 CenterZ=0 NormalX=0 NormalY=0 NormalZ=1 AngleXU=0 Radius=2 StartAngle=3.14159 EndAngle=4.71239
    g1: ArcOfCircle CenterX=2 CenterY=-108.7 CenterZ=0 NormalX=0 NormalY=0 NormalZ=1 AngleXU=0 Radius=2 StartAngle=1.5708 EndAngle=3.14159
    g2: LineSegment StartX=0 StartY=-108.7 StartZ=0 EndX=0 EndY=108.7 EndZ=0
    g3: LineSegment StartX=2 StartY=106.7 StartZ=0 EndX=2 EndY=-106.7 EndZ=0
  constraints (10):
    c: Coincident(g0,g3)
    c: Perpendicular(g3,g1) = 4.71239
    c: Perpendicular(g0,g3)
    c: Tangent(g1,g2) = 1.5708
    c: Vertical(g2)
    c: Symmetric(g1,g0,g-1)
    c: DistanceY(g3,g3) = 213.4
    c: Radius(g1) = 2
    c: PointOnObject(g-1,g2)
    c: Tangent(g0,g2) = 1.5708
FEATURE [Sketcher::SketchObject] Sketch067
  AttachmentOffset = pos=(0,0,0) rot=(0,1,0;1.5708rad)
  FullyConstrained = true
  MapMode = 7
  Placement = pos=(299.412,134.005,0) rot=(0.889126,0.323616,0.323616;1.68804rad)
  sketch-geometry (3):
    g0: ArcOfCircle CenterX=3 CenterY=3 CenterZ=0 NormalX=0 NormalY=0 NormalZ=1 AngleXU=0 Radius=3 StartAngle=3.14159 EndAngle=4.71239
    g1: LineSegment StartX=0 StartY=3 StartZ=0 EndX=0 EndY=0 EndZ=0
    g2: LineSegment StartX=0 StartY=0 StartZ=0 EndX=3 EndY=0 EndZ=0
  constraints (7):
    c: Coincident(g1,g2)
    c: Tangent(g0,g1) = -1.5708
    c: Tangent(g2,g0) = -1.5708
    c: Coincident(g1,g-1)
    c: Vertical(g1)
    c: Horizontal(g2)
    c: Radius(g0) = 3
FEATURE [Sketcher::SketchObject] Sketch068
  AttachmentOffset = pos=(0,0,0) rot=(0,1,0;1.5708rad)
  FullyConstrained = true
  MapMode = 7
  Placement = pos=(263.568,197.924,0) rot=(-0.186157,0.694747,0.694747;3.50969rad)
  sketch-geometry (3):
    g0: LineSegment StartX=0 StartY=3 StartZ=0 EndX=0 EndY=0 EndZ=0
    g1: LineSegment StartX=0 StartY=0 StartZ=0 EndX=-3 EndY=0 EndZ=0
    g2: ArcOfCircle CenterX=-3 CenterY=3 CenterZ=0 NormalX=0 NormalY=0 NormalZ=1 AngleXU=0 Radius=3 StartAngle=4.71239 EndAngle=6.28319
  constraints (7):
    c: PointOnObject(g0,g-2)
    c: Coincident(g0,g-1)
    c: Coincident(g0,g1)
    c: Horizontal(g1)
    c: Tangent(g2,g0) = 1.5708
    c: Tangent(g2,g1) = 1.5708
    c: Radius(g2) = 3
FEATURE [PartDesign::Plane] DatumPlane002
  AttachmentOffset = pos=(0,0,450) rot=(0,0,1;0rad)
  Length = 399.987
  MapMode = 5
  Placement = pos=(0,0,450) rot=(0,0,1;0rad)
  ResizeMode = 0
  Width = 284.925
  expr: .AttachmentOffset.Base.z = <<lamp_fix_BaseBend>>.length / 2
FEATURE [PartDesign::Pocket] Pocket018
  BaseFeature = -> BaseBend004
  Direction = (-0.642788,0.766044,2e-16)
  Length = 5
  Length2 = 5
  Profile = -> Sketch067
  ReferenceAxis = -> Sketch067 [N_Axis]
  Reversed = true
  Suppressed = false
  Type = 1
FEATURE [PartDesign::Pocket] Pocket019
  BaseFeature = -> Pocket018
  Direction = (0.5,-0.866025,0)
  Length = 5
  Length2 = 5
  Profile = -> Sketch068
  ReferenceAxis = -> Sketch068 [N_Axis]
  Reversed = true
  Suppressed = false
  Type = 0
FEATURE [PartDesign::Mirrored] Mirrored006
  BaseFeature = -> Pocket019
  MirrorPlane = -> DatumPlane002
  Originals = -> [Pocket018,Pocket019]
  Suppressed = false
FEATURE [PartDesign::CoordinateSystem] Local_CS026  label="lamp_fix_base_LCS"
  AttacherType = Attacher::AttachEngine3D
  MapMode = 5
FEATURE [PartDesign::CoordinateSystem] Local_CS028  label="lamp_fix_lamp_LCS"
  AttacherType = Attacher::AttachEngine3D
  MapMode = 2
  Placement = pos=(280.639,195.271,450) rot=(0.834817,-0.389282,-0.389282;1.75037rad)
FEATURE [PartDesign::Boolean] Boolean010
  BaseFeature = -> Mirrored006
  Group = -> [Compound018]
  Suppressed = false
  Type = 1
  UsePlacement = true
FEATURE [PartDesign::Body] Body012  label="lamp_fix"
  Group = -> [Binder016,BaseBend004,Sketch065,Sketch067,Sketch068,DatumPlane002,Pocket018,Pocket019,Mirrored006,Local_CS026,Sketch066,Boolean010,Local_CS028]
  Origin = -> Origin014
  Tip = -> Boolean010
COMPONENT P9 — recipe-attached ("lamp_fix_mirror", modeled in this document).
Construction recipe (the document's own serialized feature program — sketch geometry with constraints, then the solid features built on it; lengths are millimeters unless a unit is written):

FEATURE [PartDesign::SubShapeBinder] Binder017
  BindCopyOnChange = 0
  BindMode = 0
  ClaimChildren = true
  Context = -> Body013 [Binder017.]
  Fuse = false
  MakeFace = true
  OffsetFill = false
  OffsetIntersection = false
  OffsetJoinType = 0
  OffsetOpenResult = false
  PartialLoad = false
  Relative = true
  Support = -> [Part__Mirroring014]
  _Version = 2
FEATURE [PartDesign::FeaturePython] BaseBend005  # WARN: FeaturePython — macro-defined, semantics opaque (R4)
  BendSide = 1
  BendSketch = -> Binder017
  MidPlane = false
  Reverse = false
  Suppressed = false
  length = 900
  radius = 2
  thickness = 0.7
  expr: length = <<lamp_fix_BaseBend>>.length
  expr: radius = <<lamp_fix_BaseBend>>.radius
  expr: thickness = <<lamp_fix_BaseBend>>.thickness
FEATURE [PartDesign::Plane] DatumPlane003
  AttachmentOffset = pos=(0,0,450) rot=(0,0,1;0rad)
  Length = 399.511
  MapMode = 5
  Placement = pos=(0,0,450) rot=(0,0,1;0rad)
  ResizeMode = 0
  Width = 284.889
  expr: .AttachmentOffset.Base.z = <<BaseBend005>>.length / 2
FEATURE [Sketcher::SketchObject] Sketch069
  AttachmentOffset = pos=(0,0,0) rot=(0,1,0;1.5708rad)
  FullyConstrained = true
  MapMode = 7
  Placement = pos=(-299.412,134.005,0) rot=(0.249244,0.684791,0.684791;2.65306rad)
  sketch-geometry (3):
    g0: ArcOfCircle CenterX=3 CenterY=3 CenterZ=0 NormalX=0 NormalY=0 NormalZ=1 AngleXU=0 Radius=3 StartAngle=3.14159 EndAngle=4.71239
    g1: LineSegment StartX=2.6446e-12 StartY=3 StartZ=0 EndX=0 EndY=0 EndZ=0
    g2: LineSegment StartX=0 StartY=0 StartZ=0 EndX=3 EndY=2.6446e-12 EndZ=0
  constraints (7):
    c: Coincident(g1,g2)
    c: Tangent(g2,g0) = -1.5708
    c: Tangent(g0,g1) = -1.5708
    c: Coincident(g1,g-1)
    c: PointOnObject(g0,g-1)
    c: PointOnObject(g0,g-2)
    c: Radius(g0) = 3
FEATURE [Sketcher::SketchObject] Sketch070
  AttachmentOffset = pos=(0,0,0) rot=(0,1,0;1.5708rad)
  FullyConstrained = true
  MapMode = 7
  Placement = pos=(-263.568,197.924,0) rot=(0.935113,-0.250563,-0.250563;1.63783rad)
  sketch-geometry (3):
    g0: LineSegment StartX=-3 StartY=2.571e-13 StartZ=0 EndX=0 EndY=0 EndZ=0
    g1: LineSegment StartX=0 StartY=0 StartZ=0 EndX=0 EndY=3 EndZ=0
    g2: ArcOfCircle CenterX=-3 CenterY=3 CenterZ=0 NormalX=0 NormalY=0 NormalZ=1 AngleXU=0 Radius=3 StartAngle=4.71239 EndAngle=6.28319
  constraints (7):
    c: Coincident(g0,g-1)
    c: Coincident(g0,g1)
    c: Tangent(g2,g0) = -1.5708
    c: Tangent(g2,g1) = -1.5708
    c: Radius(g2) = 3
    c: PointOnObject(g1,g-2)
    c: PointOnObject(g0,g-1)
FEATURE [PartDesign::CoordinateSystem] Local_CS027
  AttacherType = Attacher::AttachEngine3D
  MapMode = 5
FEATURE [PartDesign::Pocket] Pocket027
  BaseFeature = -> BaseBend005
  Direction = (-0.642788,-0.766044,-2e-16)
  Length = 5
  Length2 = 5
  Midplane = true
  Profile = -> Sketch069
  ReferenceAxis = -> Sketch069 [N_Axis]
  Suppressed = false
  Type = 0
FEATURE [PartDesign::Pocket] Pocket021
  BaseFeature = -> Pocket027
  Direction = (0.5,0.866025,0)
  Length = 5
  Length2 = 5
  Midplane = true
  Profile = -> Sketch070
  ReferenceAxis = -> Sketch070 [N_Axis]
  Suppressed = false
  Type = 0
FEATURE [PartDesign::Mirrored] Mirrored007
  BaseFeature = -> Pocket021
  MirrorPlane = -> DatumPlane003
  Originals = -> [Pocket027,Pocket021]
  Suppressed = false
FEATURE [PartDesign::Boolean] Boolean011
  BaseFeature = -> Mirrored007
  Group = -> [Compound019]
  Suppressed = false
  Type = 1
  UsePlacement = true
FEATURE [PartDesign::Body] Body013  label="lamp_fix_mirror"
  Group = -> [Binder017,BaseBend005,DatumPlane003,Sketch069,Sketch070,Pocket027,Pocket021,Mirrored007,Boolean011,Local_CS027]
  Origin = -> Origin015
  Tip = -> Pocket027
COMPONENT P10 — recipe-attached ("Body016", modeled in this document).
Construction recipe (the document's own serialized feature program — sketch geometry with constraints, then the solid features built on it; lengths are millimeters unless a unit is written):

FEATURE [Sketcher::SketchObject] Sketch079
  FullyConstrained = true
  MapMode = 5
  sketch-geometry (5):
    g0: LineSegment StartX=-1.6 StartY=-50 StartZ=0 EndX=1.6 EndY=-50 EndZ=0
    g1: LineSegment StartX=1.6 StartY=-50 StartZ=0 EndX=1.6 EndY=50 EndZ=0
    g2: LineSegment StartX=1.6 StartY=50 StartZ=0 EndX=-1.6 EndY=50 EndZ=0
    g3: LineSegment StartX=-1.6 StartY=50 StartZ=0 EndX=-1.6 EndY=-50 EndZ=0
    g4: GeomPoint X=0 Y=0 Z=0
  constraints (12):
    c: Coincident(g0,g1)
    c: Coincident(g1,g2)
    c: Coincident(g2,g3)
    c: Coincident(g3,g0)
    c: Horizontal(g0)
    c: Horizontal(g2)
    c: Vertical(g1)
    c: Vertical(g3)
    c: Symmetric(g2,g0,g4)
    c: Coincident(g4,g-1)
    c: DistanceX(g0,g0) = 3.2
    c: DistanceY(g1,g1) = 100
FEATURE [PartDesign::Pad] Pad018
  Direction = (0,0,1)
  Length = 2.4
  Length2 = 10
  Profile = -> Sketch079
  ReferenceAxis = -> Sketch079 [N_Axis]
  Suppressed = false
  Type = 0
FEATURE [PartDesign::Boolean] Boolean015
  BaseFeature = -> Pad018
  Group = -> [Fusion002]
  Refine = true
  Suppressed = false
  Type = 0
  UsePlacement = true
FEATURE [PartDesign::Body] Body016
  Group = -> [Sketch079,Pad018,Boolean015]
  Origin = -> Origin018
  Tip = -> Boolean015
COMPONENT P11 — recipe-attached ("drain_holder", modeled in this document).
Construction recipe (the document's own serialized feature program — sketch geometry with constraints, then the solid features built on it; lengths are millimeters unless a unit is written):

FEATURE [PartDesign::SubShapeBinder] Binder021
  BindCopyOnChange = 0
  BindMode = 0
  ClaimChildren = true
  Context = -> Body017 [Binder021.]
  Fuse = false
  MakeFace = true
  OffsetFill = false
  OffsetIntersection = false
  OffsetJoinType = 0
  OffsetOpenResult = false
  PartialLoad = false
  Placement = pos=(0,0,-10) rot=(0,0,1;0rad)
  Relative = false
  Support = -> [Connect007]
  _Version = 2
FEATURE [PartDesign::FeaturePython] BaseBend006  label="drain_holder_BaseBend"  # WARN: FeaturePython — macro-defined, semantics opaque (R4)
  BendSide = 0
  BendSketch = -> Binder021
  MidPlane = false
  Reverse = false
  Suppressed = false
  length = 110
  radius = 0.1
  thickness = 0.3
FEATURE [PartDesign::CoordinateSystem] Local_CS033  label="drain_holder_LCS"
  AttacherType = Attacher::AttachEngine3D
  MapMode = 5
FEATURE [Sketcher::SketchObject] Sketch097
  AttachmentOffset = pos=(0,0,0) rot=(0,1,0;1.5708rad)
  AttachmentSupport = -> [Binder021]
  FullyConstrained = true
  MapMode = 7
  Placement = pos=(86.1933,81.5915,-10) rot=(-0.889126,0.323616,0.323616;4.59514rad)
  expr: Constraints[9] = <<drain_holder_BaseBend>>.length
  sketch-geometry (9):
    g0: ArcOfCircle CenterX=-13 CenterY=5 CenterZ=0 NormalX=0 NormalY=0 NormalZ=1 AngleXU=0 Radius=5 StartAngle=4.71239 EndAngle=6.28319
    g1: LineSegment StartX=-13 StartY=0 StartZ=0 EndX=0 EndY=0 EndZ=0
    g2: LineSegment StartX=0 StartY=0 StartZ=0 EndX=0 EndY=110 EndZ=0
    g3: ArcOfCircle CenterX=-6 CenterY=105 CenterZ=0 NormalX=0 NormalY=0 NormalZ=1 AngleXU=0 Radius=5 StartAngle=-9e-16 EndAngle=1.5708
    g4: LineSegment StartX=-6 StartY=110 StartZ=0 EndX=0 EndY=110 EndZ=0
    g5: LineSegment StartX=-1 StartY=105 StartZ=0 EndX=-1 EndY=74.5394 EndZ=0
    g6: LineSegment StartX=-8 StartY=65 StartZ=0 EndX=-8 EndY=5 EndZ=0
    g7: ArcOfCircle CenterX=-6 CenterY=74.5394 CenterZ=0 NormalX=0 NormalY=0 NormalZ=1 AngleXU=0 Radius=5 StartAngle=5.01708 EndAngle=6.28319
    g8: ArcOfCircle CenterX=-3 CenterY=65 CenterZ=0 NormalX=0 NormalY=0 NormalZ=1 AngleXU=0 Radius=5 StartAngle=1.87549 EndAngle=3.14159
  constraints (23):
    c: PointOnObject(g0,g-1)
    c: Coincident(g1,g2)
    c: Tangent(g0,g1) = -1.5708
    c: Coincident(g1,g-1)
    c: Radius(g0) = 5  'r'
    c: Horizontal(g4)
    c: Coincident(g2,g4)
    c: Vertical(g2)
    c: Tangent(g3,g4) = 1.5708
    c: DistanceY(g2) = 110
    c: Equal(g3,g0)
    c: DistanceX(g0,g1) = 8
    c: Vertical(g5)
    c: Vertical(g6)
    c: DistanceX(g3) = -1
    c: Tangent(g8,g6) = -1.5708
    c: Tangent(g8,g7) = 1.5708
    c: Tangent(g7,g5) = 1.5708
    c: DistanceY(g8) = 65
    c: Equal(g8,g7)
    c: Radius(g8) = 5
    c: Tangent(g6,g0) = 1.5708
    c: Tangent(g5,g3) = 1.5708
FEATURE [PartDesign::Plane] DatumPlane006
  AttachmentOffset = pos=(0,0,45) rot=(0,0,1;0rad)
  Length = 201.494
  MapMode = 5
  Placement = pos=(0,0,45) rot=(0,0,1;0rad)
  ResizeMode = 0
  Width = 159.874
  expr: .AttachmentOffset.Base.z = <<drain_holder_BaseBend>>.length / 2 + <<Binder021>>.Placement.Base.z
FEATURE [PartDesign::Pocket] Pocket029
  BaseFeature = -> BaseBend006
  Direction = (0.642788,0.766044,2e-16)
  Length = 5
  Length2 = 5
  Midplane = true
  Profile = -> Sketch097
  ReferenceAxis = -> Sketch097 [N_Axis]
  Suppressed = false
  Type = 0
FEATURE [PartDesign::Mirrored] Mirrored011
  MirrorPlane = -> YZ_Plane019
  Suppressed = false
FEATURE [PartDesign::MultiTransform] MultiTransform005
  BaseFeature = -> Pocket029
  Originals = -> [Pocket029]
  Refine = true
  Suppressed = false
  Transformations = -> [Mirrored011]
FEATURE [PartDesign::Boolean] Boolean016
  BaseFeature = -> MultiTransform005
  Group = -> [Compound022]
  Suppressed = false
  Type = 1
  UsePlacement = true
FEATURE [Sketcher::SketchObject] Sketch120
  AttachmentSupport = -> [XY_Plane019]
  FullyConstrained = false
  MapMode = 5
  sketch-geometry (4):
    g0: LineSegment StartX=0 StartY=0 StartZ=0 EndX=41.242 EndY=0 EndZ=0
    g1: LineSegment StartX=41.242 StartY=0 StartZ=0 EndX=41.242 EndY=52.3792 EndZ=0
    g2: LineSegment StartX=41.242 StartY=52.3792 StartZ=0 EndX=0 EndY=52.3792 EndZ=0
    g3: LineSegment StartX=0 StartY=52.3792 StartZ=0 EndX=0 EndY=0 EndZ=0
  constraints (9):
    c: Coincident(g0,g1)
    c: Coincident(g1,g2)
    c: Coincident(g2,g3)
    c: Coincident(g3,g0)
    c: Horizontal(g0)
    c: Horizontal(g2)
    c: Vertical(g1)
    c: Vertical(g3)
    c: Coincident(g0,g-1)
FEATURE [PartDesign::Body] Body017  label="drain_holder"
  Group = -> [Binder021,BaseBend006,DatumPlane006,Pocket029,MultiTransform005,Mirrored011,Boolean016,Local_CS033,Sketch097,Sketch120]
  Origin = -> Origin019
  Tip = -> Boolean016
COMPONENT P12 — recipe-attached ("cap_outer", modeled in this document).
Construction recipe (the document's own serialized feature program — sketch geometry with constraints, then the solid features built on it; lengths are millimeters unless a unit is written):

FEATURE [PartDesign::SubShapeBinder] Binder022
  BindCopyOnChange = 0
  BindMode = 0
  ClaimChildren = true
  Context = -> Body018 [Binder022.]
  Fuse = false
  MakeFace = true
  OffsetFill = false
  OffsetIntersection = false
  OffsetJoinType = 0
  OffsetOpenResult = false
  PartialLoad = false
  Relative = false
  Support = -> [Sketch081]
  _Version = 2
FEATURE [PartDesign::FeaturePython] BaseBend007  label="cap_outer_BaseBend"  # WARN: FeaturePython — macro-defined, semantics opaque (R4)
  BendSide = 1
  BendSketch = -> Binder022
  MidPlane = false
  Reverse = false
  Suppressed = false
  length = 50
  radius = 0.1
  thickness = 0.3
FEATURE [PartDesign::FeaturePython] Bend005  # WARN: FeaturePython — macro-defined, semantics opaque (R4)
  AutoMiter = false
  BaseFeature = -> BaseBend007
  BendType = 1
  LengthList = [155]
  LengthSpec = 1
  ReliefFactor = 0.7
  Suppressed = false
  UseReliefFactor = false
  angle = 90
  baseObject = -> BaseBend007 [Edge43,Edge29,Edge14]
  bendAList = [90]
  extend1 = 0
  extend2 = 0
  gap1 = 0
  gap2 = 0
  invert = true
  kfactor = 0.5
  length = 155
  maxExtendDist = 5
  minGap = 0.2
  minReliefGap = 1
  miterangle1 = 0
  miterangle2 = 0
  offset = 0
  radius = 0.1
  reliefType = 0
  reliefd = 1
  reliefw = 0.8
  sketchflip = false
  sketchinvert = false
  unfold = false
  expr: length = <<cap_outer_base_Sketch>>.Constraints.depth
  expr: radius = BaseBend007.radius
FEATURE [PartDesign::SubShapeBinder] Binder023
  BindCopyOnChange = 0
  BindMode = 0
  ClaimChildren = true
  Context = -> Body018 [Binder023.]
  Fuse = true
  MakeFace = true
  OffsetFill = false
  OffsetIntersection = false
  OffsetJoinType = 0
  OffsetOpenResult = false
  PartialLoad = false
  Placement = pos=(0,0,50) rot=(0,0,1;0rad)
  Relative = false
  Support = -> [Part__Mirroring019,Offset2D]
  _Version = 2
  expr: .Placement.Base.z = <<cap_outer_BaseBend>>.length
FEATURE [PartDesign::Pocket] Pocket025
  BaseFeature = -> Bend005
  Direction = (0,0,1)
  Length = 0.8
  Length2 = 5
  Midplane = true
  Profile = -> Binder023
  Refine = true
  Suppressed = false
  Type = 0
FEATURE [PartDesign::SubShapeBinder] Binder024
  BindCopyOnChange = 0
  BindMode = 0
  ClaimChildren = true
  Context = -> Body018 [Binder024.]
  Fuse = false
  MakeFace = true
  OffsetFill = false
  OffsetIntersection = false
  OffsetJoinType = 0
  OffsetOpenResult = false
  PartialLoad = false
  Placement = pos=(0,0,50) rot=(0,0,1;0rad)
  Relative = true
  Support = -> [CapCornerCut]
  _Version = 2
  expr: Placement = <<Binder023>>.Placement
FEATURE [PartDesign::Pocket] Pocket026
  BaseFeature = -> Pocket025
  Direction = (0,0,1)
  Length = 0.8
  Length2 = 5
  Midplane = true
  Profile = -> Binder024
  Suppressed = false
  Type = 0
  expr: Length = <<Pocket025>>.Length
FEATURE [PartDesign::CoordinateSystem] Local_CS030  label="cap_outer_LCS"
  AttacherType = Attacher::AttachEngine3D
  MapMode = 5
FEATURE [PartDesign::Boolean] Boolean017
  BaseFeature = -> Pocket026
  Group = -> [Compound023]
  Suppressed = false
  Type = 1
  UsePlacement = true
FEATURE [PartDesign::Body] Body018  label="cap_outer"
  Group = -> [Binder022,BaseBend007,Bend005,Binder023,Pocket025,Binder024,Pocket026,Boolean017,Local_CS030]
  Origin = -> Origin020
  Tip = -> Boolean017
COMPONENT P13 — recipe-attached ("cap_inner", modeled in this document).
Construction recipe (the document's own serialized feature program — sketch geometry with constraints, then the solid features built on it; lengths are millimeters unless a unit is written):

FEATURE [PartDesign::SubShapeBinder] Binder025
  BindCopyOnChange = 0
  BindMode = 0
  ClaimChildren = true
  Context = -> Body019 [Binder025.]
  Fuse = false
  MakeFace = true
  OffsetFill = false
  OffsetIntersection = false
  OffsetJoinType = 0
  OffsetOpenResult = false
  PartialLoad = false
  Relative = false
  Support = -> [Sketch084]
  _Version = 2
FEATURE [PartDesign::FeaturePython] BaseBend008  label="cap_inner_BaseBend"  # WARN: FeaturePython — macro-defined, semantics opaque (R4)
  BendSide = 0
  BendSketch = -> Binder025
  MidPlane = false
  Placement = pos=(0,0,46.7) rot=(0,0,1;0rad)
  Reverse = false
  Suppressed = false
  length = 100
  radius = 0.1
  thickness = 0.3
  expr: .Placement.Base.z = <<cap_outer_BaseBend>>.length - 3.3 mm
FEATURE [PartDesign::FeaturePython] Bend006  # WARN: FeaturePython — macro-defined, semantics opaque (R4)
  AutoMiter = true
  BaseFeature = -> BaseBend008
  BendType = 1
  LengthList = [47]
  LengthSpec = 1
  ReliefFactor = 0.7
  Suppressed = false
  UseReliefFactor = false
  angle = 90
  baseObject = -> BaseBend008 [Edge13]
  bendAList = [90]
  extend1 = 0
  extend2 = 0
  gap1 = 0
  gap2 = 0
  invert = true
  kfactor = 0.5
  length = 47
  maxExtendDist = 5
  minGap = 0.2
  minReliefGap = 1
  miterangle1 = 0
  miterangle2 = 0
  offset = 0
  radius = 0.1
  reliefType = 0
  reliefd = 1
  reliefw = 0.8
  sketchflip = false
  sketchinvert = false
  unfold = false
  expr: length = <<cap_outer_BaseBend>>.length - 3 mm
  expr: radius = BaseBend008.radius
FEATURE [PartDesign::SubShapeBinder] Binder026
  BindCopyOnChange = 0
  BindMode = 0
  ClaimChildren = false
  Context = -> Body019 [Binder026.]
  Fuse = false
  MakeFace = true
  OffsetFill = false
  OffsetIntersection = false
  OffsetJoinType = 0
  OffsetOpenResult = false
  PartialLoad = false
  Relative = true
  Support = -> [Sketch027[Edge3]]
  _Version = 2
FEATURE [Sketcher::SketchObject] Sketch085
  AttachmentOffset = pos=(0,0,636.126) rot=(0,0,1;0rad)
  ExternalGeometry = -> [Binder026]
  FullyConstrained = true
  MapMode = 5
  Placement = pos=(636.126,0,0) rot=(0.57735,0.57735,0.57735;2.0944rad)
  expr: .AttachmentOffset.Base.z = <<cap_inner_sketch>>.Constraints.side
  sketch-geometry (8):
    g0: LineSegment StartX=73.05 StartY=0 StartZ=0 EndX=73.05 EndY=-2 EndZ=0
    g1: LineSegment StartX=73.05 StartY=-2 StartZ=0 EndX=70.55 EndY=-4.5 EndZ=0
    g2: LineSegment StartX=70.55 StartY=-4.5 StartZ=0 EndX=61.55 EndY=-4.5 EndZ=0
    g3: LineSegment StartX=61.55 StartY=-4.5 StartZ=0 EndX=59.05 EndY=-2 EndZ=0
    g4: LineSegment StartX=59.05 StartY=-2 StartZ=0 EndX=59.05 EndY=0 EndZ=0
    g5: LineSegment StartX=73.05 StartY=0 StartZ=0 EndX=59.05 EndY=0 EndZ=0
    g6: LineSegment StartX=76.05 StartY=0 StartZ=0 EndX=73.05 EndY=0 EndZ=0
    g7: LineSegment StartX=59.05 StartY=0 StartZ=0 EndX=56.05 EndY=0 EndZ=0
  constraints (22):
    c: Vertical(g0)
    c: Coincident(g0,g1)
    c: Coincident(g1,g2)
    c: Horizontal(g2)
    c: Coincident(g2,g3)
    c: Coincident(g3,g4)
    c: Vertical(g4)
    c: Equal(g4,g0)
    c: Equal(g1,g3)
    c: DistanceY(g2,g4) = 4.5
    c: DistanceY(g4,g4) = 2
    c: Coincident(g0,g5)
    c: Coincident(g5,g4)
    c: PointOnObject(g4,g-3)
    c: PointOnObject(g0,g-3)
    c: Coincident(g6,g-3)
    c: Coincident(g6,g0)
    c: Coincident(g7,g4)
    c: Coincident(g7,g-3)
    c: Equal(g7,g6)
    c: DistanceX(g7,g4) = 3
    c: Angle(g3) = 2.35619
FEATURE [PartDesign::CoordinateSystem] Local_CS031  label="cap_inner_LCS"
  AttacherType = Attacher::AttachEngine3D
  MapMode = 5
FEATURE [PartDesign::FeaturePython] Bend011  # WARN: FeaturePython — macro-defined, semantics opaque (R4)
  AutoMiter = true
  BaseFeature = -> Bend006
  BendType = 1
  LengthList = [81]
  LengthSpec = 1
  ReliefFactor = 0.7
  Suppressed = false
  UseReliefFactor = false
  angle = 90
  baseObject = -> Bend006 [Edge4]
  bendAList = [90]
  extend1 = 0
  extend2 = 0
  gap1 = 3
  gap2 = 4
  invert = false
  kfactor = 0.5
  length = 81
  maxExtendDist = 5
  minGap = 0.2
  minReliefGap = 1
  miterangle1 = 0
  miterangle2 = 0
  offset = 0
  radius = 0.1
  reliefType = 0
  reliefd = 1
  reliefw = 0.8
  sketchflip = false
  sketchinvert = false
  unfold = false
  expr: radius = <<cap_outer_BaseBend>>.radius
FEATURE [PartDesign::FeaturePython] Bend012  # WARN: FeaturePython — macro-defined, semantics opaque (R4)
  AutoMiter = true
  BaseFeature = -> Bend011
  BendType = 0
  LengthList = [30]
  LengthSpec = 0
  ReliefFactor = 0.7
  Suppressed = false
  UseReliefFactor = false
  angle = 90
  baseObject = -> Bend011 [Edge3]
  bendAList = [90]
  extend1 = 0
  extend2 = 0
  gap1 = 3.2
  gap2 = 0
  invert = false
  kfactor = 0.5
  length = 30
  maxExtendDist = 5
  minGap = 0.2
  minReliefGap = 1
  miterangle1 = 0
  miterangle2 = 0
  offset = 0
  radius = 0.1
  reliefType = 0
  reliefd = 1
  reliefw = 0.8
  sketchflip = false
  sketchinvert = false
  unfold = false
  expr: radius = <<cap_outer_BaseBend>>.radius
FEATURE [PartDesign::Boolean] Boolean018
  BaseFeature = -> Bend012
  Group = -> [Compound024]
  Suppressed = false
  Type = 1
  UsePlacement = true
FEATURE [PartDesign::Pad] Pad019
  BaseFeature = -> Boolean018
  Direction = (1,0,0)
  Length = 0.3
  Length2 = 10
  Profile = -> Sketch085
  ReferenceAxis = -> Sketch085 [N_Axis]
  Refine = true
  Reversed = true
  Suppressed = false
  Type = 0
FEATURE [PartDesign::Body] Body019  label="cap_inner"
  Group = -> [Binder025,BaseBend008,Bend006,Bend011,Bend012,Boolean018,Sketch085,Binder026,Pad019,Local_CS031]
  Origin = -> Origin021
  Tip = -> Pad019
COMPONENT P14 — recipe-attached ("top_triangle", modeled in this document).
Construction recipe (the document's own serialized feature program — sketch geometry with constraints, then the solid features built on it; lengths are millimeters unless a unit is written):

FEATURE [PartDesign::SubShapeBinder] Binder027
  BindCopyOnChange = 0
  BindMode = 0
  ClaimChildren = true
  Context = -> Body020 [Binder027.]
  Fuse = false
  MakeFace = true
  OffsetFill = false
  OffsetIntersection = false
  OffsetJoinType = 0
  OffsetOpenResult = false
  PartialLoad = false
  Relative = true
  Support = -> [Sketch088]
  _Version = 2
FEATURE [PartDesign::Pad] Pad020
  Direction = (0,0,1)
  Length = 0.3
  Length2 = 10
  Profile = -> Binder027
  Suppressed = false
  Type = 0
FEATURE [PartDesign::Boolean] Boolean020
  BaseFeature = -> Pad020
  Group = -> [Compound027]
  Suppressed = false
  Type = 1
  UsePlacement = true
FEATURE [PartDesign::Body] Body020  label="top_triangle"
  Group = -> [Binder027,Pad020,Boolean020]
  Origin = -> Origin022
  Tip = -> Boolean020
COMPONENT P15 — recipe-attached ("electric_shield", modeled in this document).
Construction recipe (the document's own serialized feature program — sketch geometry with constraints, then the solid features built on it; lengths are millimeters unless a unit is written):

FEATURE [PartDesign::SubShapeBinder] Binder028
  BindCopyOnChange = 0
  BindMode = 0
  ClaimChildren = true
  Context = -> Body021 [Binder028.]
  Fuse = false
  MakeFace = true
  OffsetFill = false
  OffsetIntersection = false
  OffsetJoinType = 0
  OffsetOpenResult = false
  PartialLoad = false
  Relative = false
  Support = -> [Sketch089]
  _Version = 2
FEATURE [PartDesign::FeaturePython] BaseBend009  # WARN: FeaturePython — macro-defined, semantics opaque (R4)
  BendSide = 0
  BendSketch = -> Binder028
  MidPlane = false
  Reverse = false
  Suppressed = false
  length = 100
  radius = 0.1
  thickness = 0.3
FEATURE [PartDesign::FeaturePython] Bend007  # WARN: FeaturePython — macro-defined, semantics opaque (R4)
  AutoMiter = false
  BaseFeature = -> BaseBend009
  BendType = 1
  LengthList = [30]
  LengthSpec = 1
  ReliefFactor = 0.7
  Suppressed = false
  UseReliefFactor = false
  angle = 90
  baseObject = -> BaseBend009 [Edge6,Edge9,Edge3,Edge11]
  bendAList = [90]
  extend1 = 0
  extend2 = 0
  gap1 = 0
  gap2 = 0
  invert = false
  kfactor = 0.5
  length = 30
  maxExtendDist = 5
  minGap = 0.2
  minReliefGap = 1
  miterangle1 = 0
  miterangle2 = 0
  offset = 0
  radius = 0.1
  reliefType = 0
  reliefd = 1
  reliefw = 0.8
  sketchflip = false
  sketchinvert = false
  unfold = false
  expr: radius = BaseBend009.radius
FEATURE [PartDesign::CoordinateSystem] Local_CS035  label="electric_shield_LCS"
  AttacherType = Attacher::AttachEngine3D
  AttachmentOffset = pos=(0,0,33) rot=(0,0,1;0rad)
  AttachmentSupport = -> [XY_Plane023]
  MapMode = 5
  Placement = pos=(0,0,33) rot=(0,0,1;0rad)
  expr: .AttachmentOffset.Base.z = <<Bend007>>.length + 3 mm
FEATURE [PartDesign::Boolean] Boolean021
  BaseFeature = -> Bend007
  Group = -> [Compound029]
  Suppressed = false
  Type = 1
  UsePlacement = true
FEATURE [PartDesign::Body] Body021  label="electric_shield"
  Group = -> [Binder028,BaseBend009,Bend007,Local_CS035,Boolean021]
  Origin = -> Origin023
  Tip = -> Boolean021
COMPONENT P16 — recipe-attached ("Body022", modeled in this document).
Construction recipe (the document's own serialized feature program — sketch geometry with constraints, then the solid features built on it; lengths are millimeters unless a unit is written):

FEATURE [PartDesign::SubShapeBinder] Binder029
  BindCopyOnChange = 0
  BindMode = 0
  ClaimChildren = true
  Context = -> Body022 [Binder029.]
  Fuse = false
  MakeFace = true
  OffsetFill = false
  OffsetIntersection = false
  OffsetJoinType = 0
  OffsetOpenResult = false
  PartialLoad = false
  Relative = true
  Support = -> [Offset2D001]
  _Version = 2
FEATURE [PartDesign::FeaturePython] BaseBend010  # WARN: FeaturePython — macro-defined, semantics opaque (R4)
  BendSide = 0
  BendSketch = -> Binder029
  MidPlane = false
  Reverse = true
  Suppressed = false
  length = 100
  radius = 0.1
  thickness = 0.3
FEATURE [PartDesign::FeaturePython] Bend008  # WARN: FeaturePython — macro-defined, semantics opaque (R4)
  AutoMiter = false
  BaseFeature = -> BaseBend010
  BendType = 0
  LengthList = [30]
  LengthSpec = 0
  ReliefFactor = 0.7
  Suppressed = false
  UseReliefFactor = false
  angle = 90
  baseObject = -> BaseBend010 [Edge15,Edge18,Edge21,Edge23]
  bendAList = [90]
  extend1 = 0
  extend2 = 0
  gap1 = 3
  gap2 = 3
  invert = false
  kfactor = 0.5
  length = 30
  maxExtendDist = 5
  minGap = 0.2
  minReliefGap = 1
  miterangle1 = 45
  miterangle2 = 45
  offset = 0
  radius = 0.1
  reliefType = 0
  reliefd = 0.1
  reliefw = 0.8
  sketchflip = false
  sketchinvert = false
  unfold = false
  expr: radius = BaseBend010.radius
FEATURE [PartDesign::Boolean] Boolean019
  BaseFeature = -> Bend008
  Group = -> [Compound026]
  Suppressed = false
  Type = 1
  UsePlacement = true
FEATURE [PartDesign::Body] Body022
  Group = -> [Binder029,BaseBend010,Bend008,Boolean019]
  Origin = -> Origin024
  Tip = -> Boolean019
COMPONENT P17 — recipe-attached ("bottom_cut_Body", modeled in this document).
Construction recipe (the document's own serialized feature program — sketch geometry with constraints, then the solid features built on it; lengths are millimeters unless a unit is written):

FEATURE [PartDesign::SubShapeBinder] Binder030
  BindCopyOnChange = 0
  BindMode = 0
  ClaimChildren = true
  Context = -> Body023 [Binder030.]
  Fuse = false
  MakeFace = true
  OffsetFill = false
  OffsetIntersection = false
  OffsetJoinType = 0
  OffsetOpenResult = false
  PartialLoad = false
  Relative = false
  Support = -> [Sketch044]
  _Version = 2
FEATURE [PartDesign::Pad] Pad021
  Direction = (0,0,1)
  Length = 100
  Length2 = 10
  Profile = -> Binder030
  Suppressed = false
  Type = 0
FEATURE [PartDesign::SubShapeBinder] Binder031
  BindCopyOnChange = 0
  BindMode = 0
  ClaimChildren = true
  Context = -> Body023 [Binder031.]
  Fuse = false
  MakeFace = true
  OffsetFill = false
  OffsetIntersection = false
  OffsetJoinType = 0
  OffsetOpenResult = false
  PartialLoad = false
  Placement = pos=(0,0,100) rot=(0,0,1;0rad)
  Relative = false
  Support = -> [Sketch093]
  _Version = 2
  expr: .Placement.Base.z = <<Pad021>>.Length
FEATURE [PartDesign::Pocket] Pocket028
  BaseFeature = -> Pad021
  Direction = (0,0,-1)
  Length = 30
  Length2 = 5
  Profile = -> Binder031
  Suppressed = false
  Type = 0
FEATURE [PartDesign::Fillet] Fillet
  Base = -> Pocket028 [Edge14]
  BaseFeature = -> Pocket028
  Radius = 5
  SupportTransform = false
  Suppressed = false
  UseAllEdges = false
FEATURE [PartDesign::Body] Body023  label="bottom_cut_Body"
  Group = -> [Binder030,Pad021,Binder031,Pocket028,Fillet]
  Origin = -> Origin025
  Placement = pos=(319.563,0,0) rot=(0,0,1;0rad)
  Tip = -> Fillet
  expr: .Placement.Base.x = <<mid_Sketch>>.Constraints.middle
COMPONENT P18 — recipe-attached ("drain_holder_back", modeled in this document).
Construction recipe (the document's own serialized feature program — sketch geometry with constraints, then the solid features built on it; lengths are millimeters unless a unit is written):

FEATURE [PartDesign::SubShapeBinder] Binder033
  BindCopyOnChange = 0
  BindMode = 0
  ClaimChildren = true
  Context = -> Body025 [Binder033.]
  Fuse = false
  MakeFace = true
  OffsetFill = false
  OffsetIntersection = false
  OffsetJoinType = 0
  OffsetOpenResult = false
  PartialLoad = false
  Placement = pos=(0,101.6,0) rot=(1,0,0;1.5708rad)
  Relative = false
  Support = -> [Sketch098]
  _Version = 2
  expr: .Placement.Base.y = <<drain_holder_base_sketch>>.Constraints.offset - 3.4 mm
FEATURE [PartDesign::FeaturePython] BaseBend012  # WARN: FeaturePython — macro-defined, semantics opaque (R4)
  BendSide = 0
  BendSketch = -> Binder033
  MidPlane = false
  Reverse = false
  Suppressed = false
  length = 80
  radius = 0.1
  thickness = 0.3
FEATURE [PartDesign::FeaturePython] Bend013  # WARN: FeaturePython — macro-defined, semantics opaque (R4)
  AutoMiter = true
  BaseFeature = -> BaseBend012
  BendType = 0
  LengthList = [20]
  LengthSpec = 0
  ReliefFactor = 0.7
  Suppressed = false
  UseReliefFactor = false
  angle = 90
  baseObject = -> BaseBend012 [Edge32,Edge3]
  bendAList = [90]
  extend1 = 0
  extend2 = 0
  gap1 = 4
  gap2 = 4
  invert = false
  kfactor = 0.5
  length = 20
  maxExtendDist = 5
  minGap = 0.2
  minReliefGap = 1
  miterangle1 = 0
  miterangle2 = 0
  offset = 0
  radius = 0.1
  reliefType = 0
  reliefd = 1
  reliefw = 0.8
  sketchflip = false
  sketchinvert = false
  unfold = false
  expr: radius = BaseBend012.radius
FEATURE [Sketcher::SketchObject] Sketch099
  ExternalGeometry = -> [Binder033]
  FullyConstrained = true
  MapMode = 5
  Placement = pos=(0,0,0) rot=(0.57735,0.57735,0.57735;2.0944rad)
  expr: Constraints[8] = <<BaseBend012>>.length
  sketch-geometry (3):
    g0: LineSegment StartX=21.6 StartY=57 StartZ=0 EndX=98.6 EndY=15 EndZ=0
    g1: LineSegment StartX=98.6 StartY=15 StartZ=0 EndX=21.6 EndY=15 EndZ=0
    g2: LineSegment StartX=21.6 StartY=15 StartZ=0 EndX=21.6 EndY=57 EndZ=0
  constraints (9):
    c: Coincident(g0,g1)
    c: Horizontal(g1)
    c: Coincident(g1,g2)
    c: Coincident(g2,g0)
    c: Vertical(g2)
    c: Horizontal(g0,g-3)
    c: DistanceX(g0,g-3) = 3
    c: DistanceY(g0,g-3) = 3
    c: DistanceX(g1,g-3) = 80
FEATURE [PartDesign::Pocket] Pocket030
  BaseFeature = -> Bend013
  Direction = (-1,0,0)
  Length = 5
  Length2 = 5
  Midplane = true
  Profile = -> Sketch099
  ReferenceAxis = -> Sketch099 [N_Axis]
  Suppressed = false
  Type = 1
FEATURE [PartDesign::CoordinateSystem] Local_CS036
  AttacherType = Attacher::AttachEngine3D
  MapMode = 5
FEATURE [PartDesign::Boolean] Boolean022
  BaseFeature = -> Pocket030
  Group = -> [Compound030]
  Suppressed = false
  Type = 1
  UsePlacement = true
FEATURE [PartDesign::Body] Body025  label="drain_holder_back"
  Group = -> [Binder033,BaseBend012,Bend013,Sketch099,Pocket030,Local_CS036,Boolean022]
  Origin = -> Origin027
  Tip = -> Pocket030
COMPONENT P19 — recipe-attached ("basin_shield_wall", modeled in this document).
Construction recipe (the document's own serialized feature program — sketch geometry with constraints, then the solid features built on it; lengths are millimeters unless a unit is written):

FEATURE [PartDesign::SubShapeBinder] Binder034
  BindCopyOnChange = 0
  BindMode = 0
  ClaimChildren = true
  Context = -> Body026 [Binder034.]
  Fuse = false
  MakeFace = true
  OffsetFill = false
  OffsetIntersection = false
  OffsetJoinType = 0
  OffsetOpenResult = false
  PartialLoad = false
  Relative = true
  Support = -> [Connect009]
  _Version = 2
FEATURE [PartDesign::FeaturePython] BaseBend013  # WARN: FeaturePython — macro-defined, semantics opaque (R4)
  BendSide = 0
  BendSketch = -> Binder034
  MidPlane = false
  Reverse = false
  Suppressed = false
  length = 245
  radius = 0.1
  thickness = 0.3
FEATURE [PartDesign::FeaturePython] Extend002  # WARN: FeaturePython — macro-defined, semantics opaque (R4)
  BaseFeature = -> BaseBend013
  Offset = 0.02
  Refine = true
  Suppressed = false
  UseSubtraction = false
  baseObject = -> BaseBend013 [Face1]
  gap1 = 0
  gap2 = 0
  length = 0
FEATURE [PartDesign::FeaturePython] Bend014  # WARN: FeaturePython — macro-defined, semantics opaque (R4)
  AutoMiter = true
  BaseFeature = -> Extend002
  BendType = 0
  LengthList = [20]
  LengthSpec = 1
  ReliefFactor = 0.7
  Suppressed = false
  UseReliefFactor = false
  angle = 90
  baseObject = -> Extend002 [Edge73,Edge58,Edge76,Edge29,Edge14]
  bendAList = [90]
  extend1 = 0
  extend2 = 0
  gap1 = 0
  gap2 = 0
  invert = true
  kfactor = 0.5
  length = 20
  maxExtendDist = 5
  minGap = 0.2
  minReliefGap = 1
  miterangle1 = 0
  miterangle2 = 0
  offset = 0
  radius = 0.1
  reliefType = 0
  reliefd = 1
  reliefw = 0.8
  sketchflip = false
  sketchinvert = false
  unfold = false
  expr: radius = BaseBend013.radius
FEATURE [Sketcher::SketchObject] Sketch108
  FullyConstrained = true
  MapMode = 5
  Placement = pos=(0,0,0) rot=(0.57735,0.57735,0.57735;2.0944rad)
  sketch-geometry (11):
    g0: LineSegment StartX=0 StartY=0 StartZ=0 EndX=40 EndY=0 EndZ=0
    g1: LineSegment StartX=40 StartY=0 StartZ=0 EndX=40 EndY=70 EndZ=0
    g2: LineSegment StartX=40 StartY=70 StartZ=0 EndX=0 EndY=70 EndZ=0
    g3: LineSegment StartX=0 StartY=70 StartZ=0 EndX=0 EndY=0 EndZ=0
    g4: LineSegment StartX=50 StartY=0 StartZ=0 EndX=0 EndY=0 EndZ=0
    g5: LineSegment StartX=0 StartY=0 StartZ=0 EndX=0 EndY=80 EndZ=0
    g6: ArcOfCircle CenterX=10 CenterY=80 CenterZ=0 NormalX=0 NormalY=0 NormalZ=1 AngleXU=0 Radius=10 StartAngle=3.14159 EndAngle=4.71239
    g7: ArcOfCircle CenterX=50 CenterY=10 CenterZ=0 NormalX=0 NormalY=0 NormalZ=1 AngleXU=0 Radius=10 StartAngle=3.14159 EndAngle=4.71239
    g8: ArcOfCircle CenterX=-314.75 CenterY=10 CenterZ=0 NormalX=0 NormalY=0 NormalZ=1 AngleXU=0 Radius=354.75 StartAngle=2e-16 EndAngle=0.142615
    g9: ArcOfCircle CenterX=26.5 CenterY=59 CenterZ=0 NormalX=0 NormalY=0 NormalZ=1 AngleXU=0 Radius=10 StartAngle=0.142615 EndAngle=1.44973
    g10: ArcOfCircle CenterX=10 CenterY=-76.625 CenterZ=0 NormalX=0 NormalY=0 NormalZ=1 AngleXU=0 Radius=146.625 StartAngle=1.44973 EndAngle=1.5708
  constraints (28):
    c: Coincident(g0,g1)
    c: Coincident(g1,g2)
    c: Coincident(g2,g3)
    c: Coincident(g3,g0)
    c: Horizontal(g0)
    c: Horizontal(g2)
    c: Vertical(g1)
    c: Vertical(g3)
    c: Distance(g1,g3) = 40
    c: Distance(g0,g2) = 70
    c: Coincident(g0,g-1)
    c: PointOnObject(g4,g-1)
    c: Coincident(g4,g0)
    c: Coincident(g4,g5)
    c: PointOnObject(g5,g-2)
    c: Tangent(g6,g5) = 1.5708
    c: Tangent(g7,g4) = 1.5708
    c: Tangent(g8,g7) = 1.5708
    c: Tangent(g10,g6) = 1.5708
    c: Tangent(g10,g9) = -1.5708
    c: Tangent(g9,g8) = -1.5708
    c: Equal(g6,g7)
    c: Radius(g6) = 10
    c: Tangent(g7,g1) = 1.5708
    c: Tangent(g6,g2) = 1.5708
    c: Equal(g9,g6)
    c: DistanceX(g9) = 26.5
    c: DistanceY(g9) = 59
FEATURE [PartDesign::Pocket] Pocket031
  BaseFeature = -> Bend014
  Direction = (-1,0,0)
  Length = 5
  Length2 = 5
  Midplane = true
  Profile = -> Sketch108
  ReferenceAxis = -> Sketch108 [N_Axis]
  Suppressed = false
  Type = 1
FEATURE [PartDesign::Boolean] Boolean024
  BaseFeature = -> Pocket031
  Group = -> [Compound032]
  Suppressed = false
  Type = 1
  UsePlacement = true
FEATURE [PartDesign::CoordinateSystem] Local_CS037  label="basin_shield_wall_LCS"
  AttacherType = Attacher::AttachEngine3D
  AttachmentSupport = -> [XY_Plane028]
  MapMode = 5
FEATURE [PartDesign::CoordinateSystem] Local_CS038  label="basin_shield_wall_basin_shield_top_LCS"
  AttacherType = Attacher::AttachEngine3D
  AttachmentOffset = pos=(0,0,245) rot=(0,0,1;0rad)
  AttachmentSupport = -> [XY_Plane028]
  MapMode = 5
  Placement = pos=(0,0,245) rot=(0,0,1;0rad)
  expr: .AttachmentOffset.Base.z = <<BaseBend013>>.length
FEATURE [PartDesign::Body] Body026  label="basin_shield_wall"
  Group = -> [Binder034,BaseBend013,Extend002,Bend014,Sketch108,Pocket031,Boolean024,Local_CS037,Local_CS038]
  Origin = -> Origin028
  Tip = -> Boolean024
COMPONENT P20 — recipe-attached ("basin_shield_top", modeled in this document).
Construction recipe (the document's own serialized feature program — sketch geometry with constraints, then the solid features built on it; lengths are millimeters unless a unit is written):

FEATURE [PartDesign::SubShapeBinder] Binder035
  BindCopyOnChange = 0
  BindMode = 0
  ClaimChildren = true
  Context = -> Body027 [Binder035.]
  Fuse = false
  MakeFace = true
  OffsetFill = false
  OffsetIntersection = false
  OffsetJoinType = 0
  OffsetOpenResult = false
  PartialLoad = false
  Relative = true
  Support = -> [Connect010]
  _Version = 2
FEATURE [PartDesign::FeaturePython] BaseBend014  # WARN: FeaturePython — macro-defined, semantics opaque (R4)
  BendSide = 0
  BendSketch = -> Binder035
  MidPlane = false
  Reverse = false
  Suppressed = false
  length = 100
  radius = 0.1
  thickness = 0.3
FEATURE [PartDesign::Boolean] Boolean023
  BaseFeature = -> BaseBend014
  Group = -> [Compound031]
  Refine = true
  Suppressed = false
  Type = 1
  UsePlacement = true
FEATURE [PartDesign::FeaturePython] Bend015  # WARN: FeaturePython — macro-defined, semantics opaque (R4)
  AutoMiter = false
  BaseFeature = -> Boolean023
  BendType = 0
  LengthList = [25]
  LengthSpec = 0
  ReliefFactor = 0.7
  Suppressed = false
  UseReliefFactor = false
  angle = 90
  baseObject = -> Boolean023 [Edge24,Edge26,Edge28]
  bendAList = [90]
  extend1 = 0
  extend2 = 0
  gap1 = 0
  gap2 = 0
  invert = false
  kfactor = 0.5
  length = 25
  maxExtendDist = 5
  minGap = 0.2
  minReliefGap = 1
  miterangle1 = 30
  miterangle2 = 30
  offset = 0
  radius = 0.1
  reliefType = 0
  reliefd = 1
  reliefw = 0.8
  sketchflip = false
  sketchinvert = false
  unfold = false
  expr: radius = BaseBend014.radius
FEATURE [PartDesign::Boolean] Boolean027
  BaseFeature = -> Bend015
  Group = -> [Compound035]
  Suppressed = false
  Type = 1
  UsePlacement = true
FEATURE [PartDesign::CoordinateSystem] Local_CS039  label="basin_shield_top_LCS"
  AttacherType = Attacher::AttachEngine3D
  AttachmentOffset = pos=(0,0,-3) rot=(0,0,1;0rad)
  AttachmentSupport = -> [XY_Plane029]
  MapMode = 5
  Placement = pos=(0,0,-3) rot=(0,0,1;0rad)
FEATURE [PartDesign::CoordinateSystem] Local_CS040  label="basin_shield_top_basin_shield_corrugation_LCS"
  AttacherType = Attacher::AttachEngine3D
  AttachmentSupport = -> [XY_Plane029]
  MapMode = 5
FEATURE [PartDesign::Body] Body027  label="basin_shield_top"
  Group = -> [Binder035,BaseBend014,Boolean023,Bend015,Boolean027,Local_CS039,Local_CS040]
  Origin = -> Origin029
  Tip = -> Boolean027
COMPONENT P21 — recipe-attached ("basin_shield_corrugation", modeled in this document).
Construction recipe (the document's own serialized feature program — sketch geometry with constraints, then the solid features built on it; lengths are millimeters unless a unit is written):

FEATURE [PartDesign::SubShapeBinder] Binder038
  BindCopyOnChange = 0
  BindMode = 0
  ClaimChildren = true
  Context = -> Body030 [Binder038.]
  Fuse = false
  MakeFace = true
  OffsetFill = false
  OffsetIntersection = false
  OffsetJoinType = 0
  OffsetOpenResult = false
  PartialLoad = false
  Relative = true
  Support = -> [Connect012]
  _Version = 2
FEATURE [PartDesign::FeaturePython] BaseBend017  # WARN: FeaturePython — macro-defined, semantics opaque (R4)
  BendSide = 0
  BendSketch = -> Binder038
  MidPlane = false
  Reverse = false
  Suppressed = false
  length = 292
  radius = 0.1
  thickness = 0.3
FEATURE [PartDesign::FeaturePython] Extend003  # WARN: FeaturePython — macro-defined, semantics opaque (R4)
  BaseFeature = -> BaseBend017
  Offset = 0.02
  Refine = true
  Suppressed = false
  UseSubtraction = false
  baseObject = -> BaseBend017 [Face1]
  gap1 = 0
  gap2 = 0
  length = 0
FEATURE [PartDesign::Boolean] Boolean028
  BaseFeature = -> Extend003
  Group = -> [Compound036]
  Suppressed = false
  Type = 1
  UsePlacement = true
FEATURE [PartDesign::CoordinateSystem] Local_CS041  label="basin_shield_corrugation_LCS"
  AttacherType = Attacher::AttachEngine3D
  AttachmentSupport = -> [XY_Plane032]
  MapMode = 5
FEATURE [Sketcher::SketchObject] Sketch121
  AttachmentOffset = pos=(0,292,0) rot=(0,0,1;0rad)
  AttachmentSupport = -> [YZ_Plane032]
  ExternalGeometry = -> [Binder038]
  FullyConstrained = true
  MapMode = 5
  Placement = pos=(0,0,292) rot=(0.57735,0.57735,0.57735;2.0944rad)
  expr: .AttachmentOffset.Base.y = <<BaseBend017>>.length
  sketch-geometry (8):
    g0: ArcOfCircle CenterX=92.005 CenterY=-3 CenterZ=0 NormalX=0 NormalY=0 NormalZ=1 AngleXU=0 Radius=3 StartAngle=1.5708 EndAngle=3.14159
    g1: ArcOfCircle CenterX=84.005 CenterY=-25 CenterZ=0 NormalX=0 NormalY=0 NormalZ=1 AngleXU=0 Radius=5 StartAngle=4.71239 EndAngle=6.28319
    g2: ArcOfCircle CenterX=5 CenterY=-35 CenterZ=0 NormalX=0 NormalY=0 NormalZ=1 AngleXU=0 Radius=5 StartAngle=1.5708 EndAngle=3.14159
    g3: LineSegment StartX=0 StartY=-35 StartZ=0 EndX=0 EndY=-1.421e-13 EndZ=0
    g4: LineSegment StartX=0 StartY=-1.421e-13 StartZ=0 EndX=92.005 EndY=-1.421e-13 EndZ=0
    g5: LineSegment StartX=89.005 StartY=-3 StartZ=0 EndX=89.005 EndY=-25 EndZ=0
    g6: LineSegment StartX=84.005 StartY=-30 StartZ=0 EndX=5 EndY=-30 EndZ=0
    g7: GeomPoint X=89.005 Y=-30 Z=0
  constraints (19):
    c: PointOnObject(g2,g-2)
    c: Coincident(g3,g-1)
    c: Coincident(g4,g3)
    c: Horizontal(g6)
    c: Vertical(g5)
    c: Tangent(g3,g2) = 1.5708
    c: Tangent(g6,g2) = -1.5708
    c: Tangent(g6,g1) = 1.5708
    c: Tangent(g5,g1) = 1.5708
    c: Tangent(g5,g0) = -1.5708
    c: Tangent(g4,g0) = 1.5708
    c: PointOnObject(g7,g6)
    c: PointOnObject(g7,g5)
    c: Radius(g1) = 5
    c: Equal(g1,g2)
    c: DistanceY(g7) = -30
    c: DistanceX(g0,g-3) = 2
    c: DistanceX(g7,g-3) = 5
    c: Horizontal(g4)
FEATURE [PartDesign::Pocket] Pocket034
  BaseFeature = -> Boolean028
  Direction = (-1,0,0)
  Length = 5
  Length2 = 5
  Midplane = true
  Profile = -> Sketch121
  ReferenceAxis = -> Sketch121 [N_Axis]
  Suppressed = false
  Type = 1
FEATURE [PartDesign::Body] Body030  label="basin_shield_corrugation"
  Group = -> [Binder038,BaseBend017,Extend003,Boolean028,Local_CS041,Sketch121,Pocket034]
  Origin = -> Origin032
  Tip = -> Pocket034
COMPONENT P22 — recipe-attached ("Body", modeled in this document).
Construction recipe (the document's own serialized feature program — sketch geometry with constraints, then the solid features built on it; lengths are millimeters unless a unit is written):

FEATURE [PartDesign::SubShapeBinder] Binder039
  BindCopyOnChange = 0
  BindMode = 0
  ClaimChildren = false
  Context = -> Body031 [Binder039.]
  Fuse = false
  MakeFace = true
  OffsetFill = false
  OffsetIntersection = false
  OffsetJoinType = 0
  OffsetOpenResult = false
  PartialLoad = false
  Relative = true
  Support = -> [Connect013]
  _Version = 2
FEATURE [PartDesign::Pad] Pad022
  Direction = (0,0,1)
  Length = 1
  Length2 = 10
  Profile = -> Binder039
  Refine = true
  Suppressed = false
  Type = 0
FEATURE [PartDesign::Boolean] Boolean029
  BaseFeature = -> Pad022
  Group = -> [Compound037]
  Suppressed = false
  Type = 1
  UsePlacement = true
FEATURE [PartDesign::Body] Body031  label="Body"
  Group = -> [Binder039,Pad022,Boolean029]
  Origin = -> Origin033
  Tip = -> Boolean029
COMPONENT P23 — recipe-attached ("Body032", modeled in this document).
Construction recipe (the document's own serialized feature program — sketch geometry with constraints, then the solid features built on it; lengths are millimeters unless a unit is written):

FEATURE [PartDesign::SubShapeBinder] Binder040
  BindCopyOnChange = 0
  BindMode = 0
  ClaimChildren = false
  Context = -> Body032 [Binder040.]
  Fuse = false
  MakeFace = true
  OffsetFill = false
  OffsetIntersection = false
  OffsetJoinType = 0
  OffsetOpenResult = false
  PartialLoad = false
  Relative = true
  Support = -> [Body005[LinearPattern.Face2]]
  _Version = 2
FEATURE [Sketcher::SketchObject] Sketch122
  AttachmentSupport = -> [XZ_Plane034]
  ExternalGeometry = -> [Binder040]
  FullyConstrained = true
  MapMode = 5
  Placement = pos=(0,0,0) rot=(1,0,0;1.5708rad)
  sketch-geometry (23):
    g0: LineSegment StartX=-15 StartY=36.126 StartZ=0 EndX=15 EndY=36.126 EndZ=0
    g1: LineSegment StartX=25 StartY=46.126 StartZ=0 EndX=25 EndY=1226.13 EndZ=0
    g2: LineSegment StartX=15 StartY=1236.13 StartZ=0 EndX=-15 EndY=1236.13 EndZ=0
    g3: LineSegment StartX=-25 StartY=1226.13 StartZ=0 EndX=-25 EndY=46.126 EndZ=0
    g4: ArcOfCircle CenterX=-15 CenterY=46.126 CenterZ=0 NormalX=0 NormalY=0 NormalZ=1 AngleXU=0 Radius=10 StartAngle=3.14159 EndAngle=4.71239
    g5: ArcOfCircle CenterX=15 CenterY=46.126 CenterZ=0 NormalX=0 NormalY=0 NormalZ=1 AngleXU=0 Radius=10 StartAngle=4.71239 EndAngle=6.28319
    g6: ArcOfCircle CenterX=15 CenterY=1226.13 CenterZ=0 NormalX=0 NormalY=0 NormalZ=1 AngleXU=0 Radius=10 StartAngle=7.5e-15 EndAngle=1.5708
    g7: ArcOfCircle CenterX=-15 CenterY=1226.13 CenterZ=0 NormalX=0 NormalY=0 NormalZ=1 AngleXU=0 Radius=10 StartAngle=1.5708 EndAngle=3.14159
    g8: GeomPoint X=-25 Y=36.126 Z=0
    g9: GeomPoint X=25 Y=1236.13 Z=0
    g10: GeomPoint X=0 Y=636.126 Z=0
    g11: LineSegment StartX=-11 StartY=145 StartZ=0 EndX=0 EndY=636.126 EndZ=0
    g12: LineSegment StartX=0 StartY=636.126 StartZ=0 EndX=-11 EndY=1127.25 EndZ=0
    g13: Circle CenterX=0 CenterY=67 CenterZ=0 NormalX=0 NormalY=0 NormalZ=1 AngleXU=0 Radius=1.7
    g14: Circle CenterX=0 CenterY=127 CenterZ=0 NormalX=0 NormalY=0 NormalZ=1 AngleXU=0 Radius=1.7
    g15: Circle CenterX=0 CenterY=1145.25 CenterZ=0 NormalX=0 NormalY=0 NormalZ=1 AngleXU=0 Radius=1.7
    g16: Circle CenterX=0 CenterY=1205.25 CenterZ=0 NormalX=0 NormalY=0 NormalZ=1 AngleXU=0 Radius=1.7
    g17: LineSegment StartX=-11 StartY=1223.25 StartZ=0 EndX=0 EndY=1205.25 EndZ=0
    g18: LineSegment StartX=0 StartY=1205.25 StartZ=0 EndX=0 EndY=1145.25 EndZ=0
    g19: LineSegment StartX=0 StartY=1145.25 StartZ=0 EndX=-11 EndY=1127.25 EndZ=0
    g20: LineSegment StartX=-11 StartY=145 StartZ=0 EndX=0 EndY=127 EndZ=0
    g21: LineSegment StartX=0 StartY=127 StartZ=0 EndX=0 EndY=67 EndZ=0
    g22: LineSegment StartX=0 StartY=67 StartZ=0 EndX=-11 EndY=49 EndZ=0
  constraints (53):
    c: Tangent(g0,g4) = -1.5708
    c: Tangent(g0,g5) = -1.5708
    c: Tangent(g1,g5) = -1.5708
    c: Tangent(g1,g6) = -1.5708
    c: Tangent(g2,g6) = -1.5708
    c: Tangent(g2,g7) = -1.5708
    c: Tangent(g3,g7) = -1.5708
    c: Tangent(g3,g4) = -1.5708
    c: Horizontal(g0)
    c: Horizontal(g2)
    c: Vertical(g1)
    c: Vertical(g3)
    c: Equal(g4,g5)
    c: Equal(g5,g6)
    c: Equal(g6,g7)
    c: PointOnObject(g8,g0)
    c: PointOnObject(g8,g3)
    c: PointOnObject(g9,g1)
    c: PointOnObject(g9,g2)
    c: Radius(g6) = 10
    c: Symmetric(g8,g9,g10)
    c: PointOnObject(g10,g-2)
    c: Coincident(g-3,g11)
    c: Coincident(g11,g10)
    c: Coincident(g11,g12)
    c: Coincident(g12,g-4)
    c: DistanceX(g8,g9) = 50
    c: DistanceY(g8,g9) = 1200
    c: Equal(g11,g12)
    c: PointOnObject(g13,g-2)
    c: PointOnObject(g14,g-2)
    c: PointOnObject(g15,g-2)
    c: PointOnObject(g16,g-2)
    c: Coincident(g-4,g17)
    c: Coincident(g17,g16)
    c: Coincident(g17,g18)
    c: Coincident(g18,g15)
    c: Coincident(g18,g19)
    c: Coincident(g19,g12)
    c: Coincident(g11,g20)
    c: Coincident(g20,g14)
    c: Coincident(g20,g21)
    c: Coincident(g21,g13)
    c: Coincident(g21,g22)
    c: Coincident(g22,g-3)
    c: Equal(g22,g20)
    c: DistanceY(g21,g21) = 60
    c: Equal(g13,g14)
    c: Equal(g13,g15)
    c: Equal(g13,g16)
    c: Diameter(g13) = 3.4
    c: Equal(g18,g21)
    c: Equal(g19,g17)
FEATURE [PartDesign::Pad] Pad023
  Direction = (0,-1,2e-16)
  Length = 3
  Length2 = 10
  Placement = pos=(0,0,0) rot=(1,0,0;1.5708rad)
  Profile = -> Sketch122
  ReferenceAxis = -> Sketch122 [N_Axis]
  Suppressed = false
  Type = 0
FEATURE [PartDesign::Body] Body032
  Group = -> [Binder040,Sketch122,Pad023]
  Origin = -> Origin034
  Tip = -> Pad023
